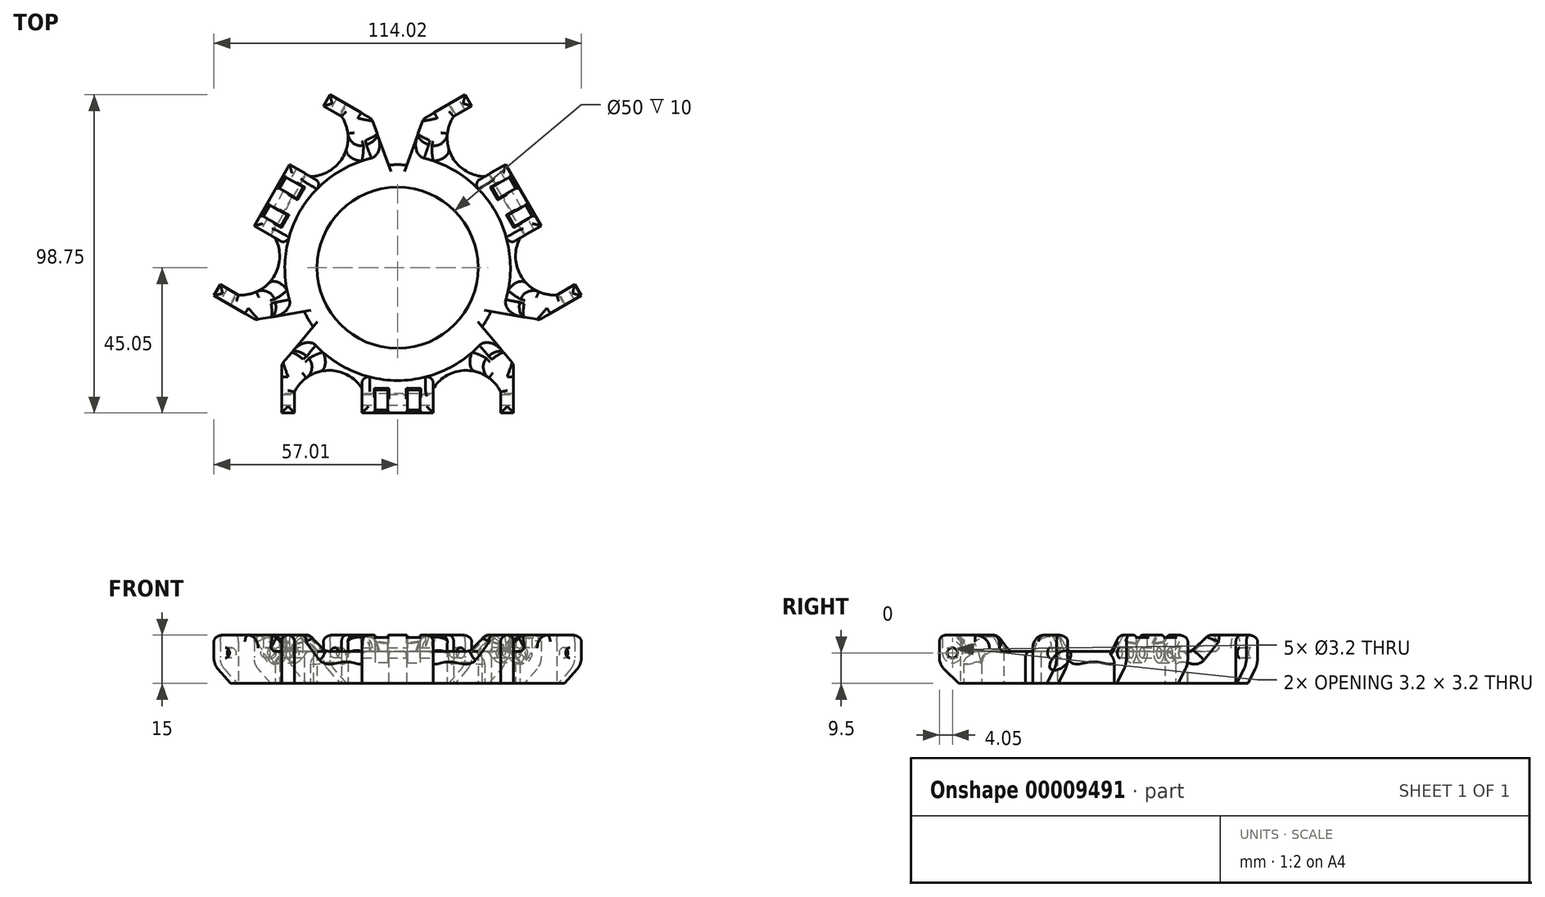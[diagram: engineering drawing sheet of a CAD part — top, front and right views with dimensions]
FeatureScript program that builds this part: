
annotation { "Feature Type Name" : "Feature", "Feature Type Description" : "" }
export const myFeature = defineFeature(function(context is Context, id is Id, definition is map)
    precondition{}
    {
        {
            assignVariable(context, id + "F0", {"name" : "JointHeight", "anyValue" : 18});
        }
        {
            var Q0;
            Q0=qCreatedBy(makeId("Top.planeOp"),FACE);
            var sketch = newSketch(context, id + "F1", { "sketchPlane" : qUnion([Q0])});
            skCircle(sketch, "E0", {"center": v(0, 0) * mm, "radius": 25 * mm});
            skCircle(sketch, "E1", {"center": v(0, 0) * mm, "radius": 32 * mm});
            skSolve(sketch);
        }
        {
            var Q0;
            Q0=qCreatedBy(makeId("Top.planeOp"),FACE);
            var sketch = newSketch(context, id + "F2", { "sketchPlane" : qUnion([Q0])});
            skLineSegment(sketch, "E2", {"start": v(-21.5, 50) * mm, "end": v(-21.5, -50) * mm, "construction": true});
            skLineSegment(sketch, "E3", {"start": v(21.5, 50) * mm, "end": v(21.5, -50) * mm, "construction": true});
            skLineSegment(sketch, "E4", {"start": v(-11, -50) * mm, "end": v(-11, -30.05) * mm, "construction": true});
            skLineSegment(sketch, "E5", {"start": v(11, -50) * mm, "end": v(11, -30.05) * mm, "construction": true});
            skLineSegment(sketch, "E6", {"start": v(-32, -50) * mm, "end": v(-32, 0) * mm, "construction": true});
            skLineSegment(sketch, "E7", {"start": v(32, -50) * mm, "end": v(32, 0) * mm, "construction": true});
            skLineSegment(sketch, "E8", {"start": v(0, -41.5) * mm, "end": v(0, -32) * mm, "construction": true});
            skLineSegment(sketch, "E9", {"start": v(-11, -30.05) * mm, "end": v(-11, -45.05) * mm});
            skLineSegment(sketch, "E10", {"start": v(-11, -45.05) * mm, "end": v(11, -45.05) * mm});
            skLineSegment(sketch, "E11", {"start": v(11, -45.05) * mm, "end": v(11, -30.05) * mm});
            skLineSegment(sketch, "E12", {"start": v(-32, -45.05) * mm, "end": v(-36, -45.05) * mm});
            skArc(sketch, "E13", {"start": v(-11, -30.05) * mm, "mid": v(0, -32) * mm, "end": v(11, -30.05) * mm});
            skLineSegment(sketch, "E14", {"start": v(-36, -45.05) * mm, "end": v(-36, -30.05) * mm});
            skLineSegment(sketch, "E15", {"start": v(-36, -30.05) * mm, "end": v(-26.2, -18.37) * mm});
            skCircle(sketch, "E16", {"center": v(-21.5, -41.5) * mm, "radius": 9.25 * mm, "construction": true});
            skLineSegment(sketch, "E17", {"start": v(-32, -45.05) * mm, "end": v(-32, -38.55) * mm});
            skArc(sketch, "E18", {"start": v(-11, -37.55) * mm, "mid": v(-21.8, -31.88) * mm, "end": v(-32, -38.55) * mm});
            skArc(sketch, "E19", {"start": v(-26.2, -18.37) * mm, "mid": v(-19.5, -25.38) * mm, "end": v(-11, -30.05) * mm});
            skLineSegment(sketch, "E20.MirrorCS", {"start": v(36, -45.05) * mm, "end": v(36, -30.05) * mm});
            skLineSegment(sketch, "E21.MirrorCS", {"start": v(32, -45.05) * mm, "end": v(36, -45.05) * mm});
            skLineSegment(sketch, "E22.MirrorCS", {"start": v(36, -30.05) * mm, "end": v(26.2, -18.37) * mm});
            skLineSegment(sketch, "E23.MirrorCS", {"start": v(32, -45.05) * mm, "end": v(32, -38.55) * mm});
            skArc(sketch, "E24.MirrorCS", {"start": v(11, -37.55) * mm, "mid": v(21.8, -31.88) * mm, "end": v(32, -38.55) * mm});
            skArc(sketch, "E25.MirrorCS", {"start": v(26.2, -18.37) * mm, "mid": v(19.5, -25.38) * mm, "end": v(11, -30.05) * mm});
            skSolve(sketch);
        }
        {
            var Q0;
            Q0=makeQuery(id+"F1.imprint","IMPRINT",FACE,{"disambiguationData":[TD([[makeQuery(id+"F1.imprint","IMPRINT",EDGE,{"derivedFrom":sQuery(id+"F1.wireOp",EDGE,"E0")}),-1.0]])]});
            extrude(context, id + "F3", {"entities" : qUnion([Q0]), "depth" : 10 * mm});
        }
        {
            var Q0;
            Q0 = qSketchRegion(id + "F2", true);
            extrude(context, id + "F4", {"entities" : qUnion([Q0]), "depth" : (getVariable(context, 'JointHeight') - 3) * mm});
        }
        {
            var Q0;
            Q0=makeQuery(id+"F4.opExtrude","SWEPT_FACE",FACE,{"disambiguationData":[OSD([sQuery(id+"F2.wireOp",EDGE,"E20.MirrorCS")])]});
            var sketch = newSketch(context, id + "F5", { "sketchPlane" : qUnion([Q0])});
            skCircle(sketch, "E26", {"center": v(-41, 9.5) * mm, "radius": 1.6 * mm});
            skSolve(sketch);
        }
        {
            var Q0;
            Q0=makeQuery(id+"F5.imprint","IMPRINT",FACE,{"disambiguationData":[TD([[makeQuery(id+"F5.imprint","IMPRINT",EDGE,{"derivedFrom":sQuery(id+"F5.wireOp",EDGE,"E26")}),1.0]])]});
            var Q1;
            Q1=makeQuery(id+"F4.opExtrude","SWEPT_FACE",FACE,{"disambiguationData":[OSD([sQuery(id+"F2.wireOp",EDGE,"E14")])]});
            extrude(context, id + "F6", {"entities" : qUnion([Q0]), "operationType" : NewBodyOperationType.REMOVE, "endBound" : BoundingType.UP_TO_SURFACE, "oppositeDirection" : true, "endBoundEntityFace" : qUnion([Q1]), "depth" : 25 * mm});
        }
        {
            var Q0;
            Q0=makeQuery(id+"F4.opExtrude","SWEPT_BODY",BODY,{"disambiguationData":[OSD([sQuery(id+"F2.wireOp",EDGE,"E9"),sQuery(id+"F2.wireOp",EDGE,"E10"),sQuery(id+"F2.wireOp",EDGE,"E11"),sQuery(id+"F2.wireOp",EDGE,"E12"),sQuery(id+"F2.wireOp",EDGE,"E13"),sQuery(id+"F2.wireOp",EDGE,"E14"),sQuery(id+"F2.wireOp",EDGE,"E15"),sQuery(id+"F2.wireOp",EDGE,"E17"),sQuery(id+"F2.wireOp",EDGE,"E18"),sQuery(id+"F2.wireOp",EDGE,"E19"),sQuery(id+"F2.wireOp",EDGE,"E20.MirrorCS"),sQuery(id+"F2.wireOp",EDGE,"E21.MirrorCS"),sQuery(id+"F2.wireOp",EDGE,"E22.MirrorCS"),sQuery(id+"F2.wireOp",EDGE,"E23.MirrorCS"),sQuery(id+"F2.wireOp",EDGE,"E24.MirrorCS"),sQuery(id+"F2.wireOp",EDGE,"E25.MirrorCS")])]});
            var Q1;
            Q1=makeQuery(id+"F3.opExtrude","SWEPT_FACE",FACE,{"disambiguationData":[OSD([sQuery(id+"F1.wireOp",EDGE,"E1")])]});
            circularPattern(context, id + "F7", {"operationType" : NewBodyOperationType.ADD, "entities" : qUnion([Q0]), "axis" : qUnion([Q1]), "angle" : 120 * degree, "instanceCount" : 3});
        }
        {
            var Q0;
            Q0=makeQuery(id+"F4.opExtrude","CAP_EDGE",EDGE,{"disambiguationData":[OSD([sQuery(id+"F2.wireOp",EDGE,"E13"),sQuery(id+"F2.wireOp",EDGE,"E19"),sQuery(id+"F2.wireOp",EDGE,"E25.MirrorCS")])],"isStart":false});
            var Q1;
            Q1=makeQuery(id+"F7.opPattern","COPY",EDGE,{"derivedFrom":makeQuery(id+"F4.opExtrude","CAP_EDGE",EDGE,{"disambiguationData":[OSD([sQuery(id+"F2.wireOp",EDGE,"E13"),sQuery(id+"F2.wireOp",EDGE,"E19"),sQuery(id+"F2.wireOp",EDGE,"E25.MirrorCS")])],"isStart":false}),"instanceName":"1"});
            var Q2;
            Q2=makeQuery(id+"F7.opPattern","COPY",EDGE,{"derivedFrom":makeQuery(id+"F4.opExtrude","CAP_EDGE",EDGE,{"disambiguationData":[OSD([sQuery(id+"F2.wireOp",EDGE,"E13"),sQuery(id+"F2.wireOp",EDGE,"E19"),sQuery(id+"F2.wireOp",EDGE,"E25.MirrorCS")])],"isStart":false}),"instanceName":"2"});
            chamfer(context, id + "F8", {"entities" : qUnion([Q0, Q1, Q2]), "width" : 8 * mm});
        }
        {
            var Q0;
            Q0=makeQuery(id+"F8.opChamfer","BLEND_EDGE",EDGE,{"blendedFrom":[makeQuery(id+"F4.opExtrude","CAP_EDGE",EDGE,{"disambiguationData":[OSD([sQuery(id+"F2.wireOp",EDGE,"E13"),sQuery(id+"F2.wireOp",EDGE,"E19"),sQuery(id+"F2.wireOp",EDGE,"E25.MirrorCS")])],"isStart":false}),makeQuery(id+"F4.opExtrude","SWEPT_FACE",FACE,{"disambiguationData":[OSD([sQuery(id+"F2.wireOp",EDGE,"E24.MirrorCS")])]})],"blendedInto":[makeQuery(id+"F4.opExtrude","SWEPT_FACE",FACE,{"disambiguationData":[OSD([sQuery(id+"F2.wireOp",EDGE,"E24.MirrorCS")])]})]});
            var Q1;
            Q1=makeQuery(id+"F8.opChamfer","BLEND_EDGE",EDGE,{"blendedFrom":[makeQuery(id+"F4.opExtrude","CAP_EDGE",EDGE,{"disambiguationData":[OSD([sQuery(id+"F2.wireOp",EDGE,"E13"),sQuery(id+"F2.wireOp",EDGE,"E19"),sQuery(id+"F2.wireOp",EDGE,"E25.MirrorCS")])],"isStart":false}),makeQuery(id+"F4.opExtrude","SWEPT_FACE",FACE,{"disambiguationData":[OSD([sQuery(id+"F2.wireOp",EDGE,"E18")])]})],"blendedInto":[makeQuery(id+"F4.opExtrude","SWEPT_FACE",FACE,{"disambiguationData":[OSD([sQuery(id+"F2.wireOp",EDGE,"E18")])]})]});
            var Q2;
            Q2=makeQuery(id+"F8.opChamfer","BLEND_EDGE",EDGE,{"blendedFrom":[makeQuery(id+"F4.opExtrude","CAP_EDGE",EDGE,{"disambiguationData":[OSD([sQuery(id+"F2.wireOp",EDGE,"E13"),sQuery(id+"F2.wireOp",EDGE,"E19"),sQuery(id+"F2.wireOp",EDGE,"E25.MirrorCS")])],"isStart":false}),makeQuery(id+"F4.opExtrude","SWEPT_FACE",FACE,{"disambiguationData":[OSD([sQuery(id+"F2.wireOp",EDGE,"E22.MirrorCS")])]})],"blendedInto":[makeQuery(id+"F4.opExtrude","SWEPT_FACE",FACE,{"disambiguationData":[OSD([sQuery(id+"F2.wireOp",EDGE,"E22.MirrorCS")])]})]});
            var Q3;
            Q3=makeQuery(id+"F8.opChamfer","BLEND_EDGE",EDGE,{"blendedFrom":[makeQuery(id+"F4.opExtrude","CAP_EDGE",EDGE,{"disambiguationData":[OSD([sQuery(id+"F2.wireOp",EDGE,"E13"),sQuery(id+"F2.wireOp",EDGE,"E19"),sQuery(id+"F2.wireOp",EDGE,"E25.MirrorCS")])],"isStart":false}),makeQuery(id+"F4.opExtrude","SWEPT_FACE",FACE,{"disambiguationData":[OSD([sQuery(id+"F2.wireOp",EDGE,"E15")])]})],"blendedInto":[makeQuery(id+"F4.opExtrude","SWEPT_FACE",FACE,{"disambiguationData":[OSD([sQuery(id+"F2.wireOp",EDGE,"E15")])]})]});
            var Q4;
            Q4=makeQuery(id+"F8.opChamfer","BLEND_EDGE",EDGE,{"blendedFrom":[makeQuery(id+"F7.opPattern","COPY",EDGE,{"derivedFrom":makeQuery(id+"F4.opExtrude","CAP_EDGE",EDGE,{"disambiguationData":[OSD([sQuery(id+"F2.wireOp",EDGE,"E13"),sQuery(id+"F2.wireOp",EDGE,"E19"),sQuery(id+"F2.wireOp",EDGE,"E25.MirrorCS")])],"isStart":false}),"instanceName":"2"}),makeQuery(id+"F7.opPattern","COPY",FACE,{"derivedFrom":makeQuery(id+"F4.opExtrude","SWEPT_FACE",FACE,{"disambiguationData":[OSD([sQuery(id+"F2.wireOp",EDGE,"E18")])]}),"instanceName":"2"})],"blendedInto":[makeQuery(id+"F7.opPattern","COPY",FACE,{"derivedFrom":makeQuery(id+"F4.opExtrude","SWEPT_FACE",FACE,{"disambiguationData":[OSD([sQuery(id+"F2.wireOp",EDGE,"E18")])]}),"instanceName":"2"})]});
            var Q5;
            Q5=makeQuery(id+"F8.opChamfer","BLEND_EDGE",EDGE,{"blendedFrom":[makeQuery(id+"F7.opPattern","COPY",EDGE,{"derivedFrom":makeQuery(id+"F4.opExtrude","CAP_EDGE",EDGE,{"disambiguationData":[OSD([sQuery(id+"F2.wireOp",EDGE,"E13"),sQuery(id+"F2.wireOp",EDGE,"E19"),sQuery(id+"F2.wireOp",EDGE,"E25.MirrorCS")])],"isStart":false}),"instanceName":"1"}),makeQuery(id+"F7.opPattern","COPY",FACE,{"derivedFrom":makeQuery(id+"F4.opExtrude","SWEPT_FACE",FACE,{"disambiguationData":[OSD([sQuery(id+"F2.wireOp",EDGE,"E24.MirrorCS")])]}),"instanceName":"1"})],"blendedInto":[makeQuery(id+"F7.opPattern","COPY",FACE,{"derivedFrom":makeQuery(id+"F4.opExtrude","SWEPT_FACE",FACE,{"disambiguationData":[OSD([sQuery(id+"F2.wireOp",EDGE,"E24.MirrorCS")])]}),"instanceName":"1"})]});
            var Q6;
            Q6=makeQuery(id+"F8.opChamfer","BLEND_EDGE",EDGE,{"blendedFrom":[makeQuery(id+"F7.opPattern","COPY",EDGE,{"derivedFrom":makeQuery(id+"F4.opExtrude","CAP_EDGE",EDGE,{"disambiguationData":[OSD([sQuery(id+"F2.wireOp",EDGE,"E13"),sQuery(id+"F2.wireOp",EDGE,"E19"),sQuery(id+"F2.wireOp",EDGE,"E25.MirrorCS")])],"isStart":false}),"instanceName":"1"}),makeQuery(id+"F7.opPattern","COPY",FACE,{"derivedFrom":makeQuery(id+"F4.opExtrude","SWEPT_FACE",FACE,{"disambiguationData":[OSD([sQuery(id+"F2.wireOp",EDGE,"E18")])]}),"instanceName":"1"})],"blendedInto":[makeQuery(id+"F7.opPattern","COPY",FACE,{"derivedFrom":makeQuery(id+"F4.opExtrude","SWEPT_FACE",FACE,{"disambiguationData":[OSD([sQuery(id+"F2.wireOp",EDGE,"E18")])]}),"instanceName":"1"})]});
            var Q7;
            Q7=makeQuery(id+"F8.opChamfer","BLEND_EDGE",EDGE,{"blendedFrom":[makeQuery(id+"F7.opPattern","COPY",EDGE,{"derivedFrom":makeQuery(id+"F4.opExtrude","CAP_EDGE",EDGE,{"disambiguationData":[OSD([sQuery(id+"F2.wireOp",EDGE,"E13"),sQuery(id+"F2.wireOp",EDGE,"E19"),sQuery(id+"F2.wireOp",EDGE,"E25.MirrorCS")])],"isStart":false}),"instanceName":"2"}),makeQuery(id+"F7.opPattern","COPY",FACE,{"derivedFrom":makeQuery(id+"F4.opExtrude","SWEPT_FACE",FACE,{"disambiguationData":[OSD([sQuery(id+"F2.wireOp",EDGE,"E24.MirrorCS")])]}),"instanceName":"2"})],"blendedInto":[makeQuery(id+"F7.opPattern","COPY",FACE,{"derivedFrom":makeQuery(id+"F4.opExtrude","SWEPT_FACE",FACE,{"disambiguationData":[OSD([sQuery(id+"F2.wireOp",EDGE,"E24.MirrorCS")])]}),"instanceName":"2"})]});
            var Q8;
            Q8=makeQuery(id+"F8.opChamfer","BLEND_EDGE",EDGE,{"blendedFrom":[makeQuery(id+"F7.opPattern","COPY",EDGE,{"derivedFrom":makeQuery(id+"F4.opExtrude","CAP_EDGE",EDGE,{"disambiguationData":[OSD([sQuery(id+"F2.wireOp",EDGE,"E13"),sQuery(id+"F2.wireOp",EDGE,"E19"),sQuery(id+"F2.wireOp",EDGE,"E25.MirrorCS")])],"isStart":false}),"instanceName":"1"}),makeQuery(id+"F7.opPattern","COPY",FACE,{"derivedFrom":makeQuery(id+"F4.opExtrude","SWEPT_FACE",FACE,{"disambiguationData":[OSD([sQuery(id+"F2.wireOp",EDGE,"E22.MirrorCS")])]}),"instanceName":"1"})],"blendedInto":[makeQuery(id+"F7.opPattern","COPY",FACE,{"derivedFrom":makeQuery(id+"F4.opExtrude","SWEPT_FACE",FACE,{"disambiguationData":[OSD([sQuery(id+"F2.wireOp",EDGE,"E22.MirrorCS")])]}),"instanceName":"1"})]});
            var Q9;
            Q9=makeQuery(id+"F8.opChamfer","BLEND_EDGE",EDGE,{"blendedFrom":[makeQuery(id+"F7.opPattern","COPY",EDGE,{"derivedFrom":makeQuery(id+"F4.opExtrude","CAP_EDGE",EDGE,{"disambiguationData":[OSD([sQuery(id+"F2.wireOp",EDGE,"E13"),sQuery(id+"F2.wireOp",EDGE,"E19"),sQuery(id+"F2.wireOp",EDGE,"E25.MirrorCS")])],"isStart":false}),"instanceName":"1"}),makeQuery(id+"F7.opPattern","COPY",FACE,{"derivedFrom":makeQuery(id+"F4.opExtrude","SWEPT_FACE",FACE,{"disambiguationData":[OSD([sQuery(id+"F2.wireOp",EDGE,"E15")])]}),"instanceName":"1"})],"blendedInto":[makeQuery(id+"F7.opPattern","COPY",FACE,{"derivedFrom":makeQuery(id+"F4.opExtrude","SWEPT_FACE",FACE,{"disambiguationData":[OSD([sQuery(id+"F2.wireOp",EDGE,"E15")])]}),"instanceName":"1"})]});
            var Q10;
            Q10=makeQuery(id+"F8.opChamfer","BLEND_EDGE",EDGE,{"blendedFrom":[makeQuery(id+"F7.opPattern","COPY",EDGE,{"derivedFrom":makeQuery(id+"F4.opExtrude","CAP_EDGE",EDGE,{"disambiguationData":[OSD([sQuery(id+"F2.wireOp",EDGE,"E13"),sQuery(id+"F2.wireOp",EDGE,"E19"),sQuery(id+"F2.wireOp",EDGE,"E25.MirrorCS")])],"isStart":false}),"instanceName":"2"}),makeQuery(id+"F7.opPattern","COPY",FACE,{"derivedFrom":makeQuery(id+"F4.opExtrude","SWEPT_FACE",FACE,{"disambiguationData":[OSD([sQuery(id+"F2.wireOp",EDGE,"E22.MirrorCS")])]}),"instanceName":"2"})],"blendedInto":[makeQuery(id+"F7.opPattern","COPY",FACE,{"derivedFrom":makeQuery(id+"F4.opExtrude","SWEPT_FACE",FACE,{"disambiguationData":[OSD([sQuery(id+"F2.wireOp",EDGE,"E22.MirrorCS")])]}),"instanceName":"2"})]});
            var Q11;
            Q11=makeQuery(id+"F7.opPattern","COPY",EDGE,{"derivedFrom":makeQuery(id+"F4.opExtrude","CAP_EDGE",EDGE,{"disambiguationData":[OSD([sQuery(id+"F2.wireOp",EDGE,"E15")])],"isStart":false}),"instanceName":"2"});
            var Q12;
            Q12=makeQuery(id+"F4.opExtrude","CAP_EDGE",EDGE,{"disambiguationData":[OSD([sQuery(id+"F2.wireOp",EDGE,"E22.MirrorCS")])],"isStart":false});
            var Q13;
            Q13=makeQuery(id+"F8.opChamfer","BLEND_EDGE",EDGE,{"blendedFrom":[makeQuery(id+"F7.opPattern","COPY",EDGE,{"derivedFrom":makeQuery(id+"F4.opExtrude","CAP_EDGE",EDGE,{"disambiguationData":[OSD([sQuery(id+"F2.wireOp",EDGE,"E13"),sQuery(id+"F2.wireOp",EDGE,"E19"),sQuery(id+"F2.wireOp",EDGE,"E25.MirrorCS")])],"isStart":false}),"instanceName":"2"}),makeQuery(id+"F7.opPattern","COPY",FACE,{"derivedFrom":makeQuery(id+"F4.opExtrude","SWEPT_FACE",FACE,{"disambiguationData":[OSD([sQuery(id+"F2.wireOp",EDGE,"E15")])]}),"instanceName":"2"})],"blendedInto":[makeQuery(id+"F7.opPattern","COPY",FACE,{"derivedFrom":makeQuery(id+"F4.opExtrude","SWEPT_FACE",FACE,{"disambiguationData":[OSD([sQuery(id+"F2.wireOp",EDGE,"E15")])]}),"instanceName":"2"})]});
            var Q14;
            {var subQ0=sQuery(id+"F1.wireOp",EDGE,"E1");Q14=makeQuery(id+"F8.opChamfer","TWEAK_EDGE",EDGE,{"derivedFrom":[makeQuery(id+"F7.boolean.opBoolean","TWEAK_VERTEX",VERTEX,{"derivedFrom":[makeQuery(id+"F3.opExtrude","CAP_FACE",FACE,{"disambiguationData":[OSD([sQuery(id+"F1.wireOp",EDGE,"E0"),subQ0])],"isStart":false}),makeQuery(id+"F3.opExtrude","SWEPT_FACE",FACE,{"disambiguationData":[OSD([subQ0])]}),makeQuery(id+"F7.opPattern","COPY",FACE,{"derivedFrom":makeQuery(id+"F4.opExtrude","SWEPT_FACE",FACE,{"disambiguationData":[OSD([sQuery(id+"F2.wireOp",EDGE,"E13"),sQuery(id+"F2.wireOp",EDGE,"E19"),sQuery(id+"F2.wireOp",EDGE,"E25.MirrorCS")])]}),"instanceName":"2"}),makeQuery(id+"F7.opPattern","COPY",FACE,{"derivedFrom":makeQuery(id+"F4.opExtrude","SWEPT_FACE",FACE,{"disambiguationData":[OSD([sQuery(id+"F2.wireOp",EDGE,"E22.MirrorCS")])]}),"instanceName":"2"})]})]});}
            var Q15;
            {var subQ0=sQuery(id+"F1.wireOp",EDGE,"E1");Q15=makeQuery(id+"F8.opChamfer","TWEAK_EDGE",EDGE,{"derivedFrom":[makeQuery(id+"F7.boolean.opBoolean","TWEAK_VERTEX",VERTEX,{"derivedFrom":[makeQuery(id+"F3.opExtrude","CAP_FACE",FACE,{"disambiguationData":[OSD([sQuery(id+"F1.wireOp",EDGE,"E0"),subQ0])],"isStart":false}),makeQuery(id+"F3.opExtrude","SWEPT_FACE",FACE,{"disambiguationData":[OSD([subQ0])]}),makeQuery(id+"F7.opPattern","COPY",FACE,{"derivedFrom":makeQuery(id+"F4.opExtrude","SWEPT_FACE",FACE,{"disambiguationData":[OSD([sQuery(id+"F2.wireOp",EDGE,"E13"),sQuery(id+"F2.wireOp",EDGE,"E19"),sQuery(id+"F2.wireOp",EDGE,"E25.MirrorCS")])]}),"instanceName":"1"}),makeQuery(id+"F7.opPattern","COPY",FACE,{"derivedFrom":makeQuery(id+"F4.opExtrude","SWEPT_FACE",FACE,{"disambiguationData":[OSD([sQuery(id+"F2.wireOp",EDGE,"E15")])]}),"instanceName":"1"})]})]});}
            var Q16;
            {var subQ0=sQuery(id+"F1.wireOp",EDGE,"E1");Q16=makeQuery(id+"F8.opChamfer","TWEAK_EDGE",EDGE,{"derivedFrom":[makeQuery(id+"F7.boolean.opBoolean","TWEAK_VERTEX",VERTEX,{"derivedFrom":[makeQuery(id+"F3.opExtrude","CAP_FACE",FACE,{"disambiguationData":[OSD([sQuery(id+"F1.wireOp",EDGE,"E0"),subQ0])],"isStart":false}),makeQuery(id+"F3.opExtrude","SWEPT_FACE",FACE,{"disambiguationData":[OSD([subQ0])]}),makeQuery(id+"F7.opPattern","COPY",FACE,{"derivedFrom":makeQuery(id+"F4.opExtrude","SWEPT_FACE",FACE,{"disambiguationData":[OSD([sQuery(id+"F2.wireOp",EDGE,"E13"),sQuery(id+"F2.wireOp",EDGE,"E19"),sQuery(id+"F2.wireOp",EDGE,"E25.MirrorCS")])]}),"instanceName":"1"}),makeQuery(id+"F7.opPattern","COPY",FACE,{"derivedFrom":makeQuery(id+"F4.opExtrude","SWEPT_FACE",FACE,{"disambiguationData":[OSD([sQuery(id+"F2.wireOp",EDGE,"E22.MirrorCS")])]}),"instanceName":"1"})]})]});}
            var Q17;
            {var subQ0=sQuery(id+"F1.wireOp",EDGE,"E1");Q17=makeQuery(id+"F8.opChamfer","TWEAK_EDGE",EDGE,{"derivedFrom":[makeQuery(id+"F7.boolean.opBoolean","TWEAK_VERTEX",VERTEX,{"derivedFrom":[makeQuery(id+"F3.opExtrude","CAP_FACE",FACE,{"disambiguationData":[OSD([sQuery(id+"F1.wireOp",EDGE,"E0"),subQ0])],"isStart":false}),makeQuery(id+"F3.opExtrude","SWEPT_FACE",FACE,{"disambiguationData":[OSD([subQ0])]}),makeQuery(id+"F4.opExtrude","SWEPT_FACE",FACE,{"disambiguationData":[OSD([sQuery(id+"F2.wireOp",EDGE,"E13"),sQuery(id+"F2.wireOp",EDGE,"E19"),sQuery(id+"F2.wireOp",EDGE,"E25.MirrorCS")])]}),makeQuery(id+"F4.opExtrude","SWEPT_FACE",FACE,{"disambiguationData":[OSD([sQuery(id+"F2.wireOp",EDGE,"E15")])]})]})]});}
            var Q18;
            Q18=makeQuery(id+"F4.opExtrude","CAP_EDGE",EDGE,{"disambiguationData":[OSD([sQuery(id+"F2.wireOp",EDGE,"E15")])],"isStart":false});
            var Q19;
            Q19=makeQuery(id+"F7.opPattern","COPY",EDGE,{"derivedFrom":makeQuery(id+"F4.opExtrude","CAP_EDGE",EDGE,{"disambiguationData":[OSD([sQuery(id+"F2.wireOp",EDGE,"E22.MirrorCS")])],"isStart":false}),"instanceName":"1"});
            var Q20;
            Q20=makeQuery(id+"F7.opPattern","COPY",EDGE,{"derivedFrom":makeQuery(id+"F4.opExtrude","CAP_EDGE",EDGE,{"disambiguationData":[OSD([sQuery(id+"F2.wireOp",EDGE,"E22.MirrorCS")])],"isStart":false}),"instanceName":"2"});
            var Q21;
            Q21=makeQuery(id+"F7.opPattern","COPY",EDGE,{"derivedFrom":makeQuery(id+"F4.opExtrude","CAP_EDGE",EDGE,{"disambiguationData":[OSD([sQuery(id+"F2.wireOp",EDGE,"E15")])],"isStart":false}),"instanceName":"1"});
            var Q22;
            {var subQ0=sQuery(id+"F1.wireOp",EDGE,"E1");Q22=makeQuery(id+"F8.opChamfer","TWEAK_EDGE",EDGE,{"derivedFrom":[makeQuery(id+"F7.boolean.opBoolean","TWEAK_VERTEX",VERTEX,{"derivedFrom":[makeQuery(id+"F3.opExtrude","CAP_FACE",FACE,{"disambiguationData":[OSD([sQuery(id+"F1.wireOp",EDGE,"E0"),subQ0])],"isStart":false}),makeQuery(id+"F3.opExtrude","SWEPT_FACE",FACE,{"disambiguationData":[OSD([subQ0])]}),makeQuery(id+"F7.opPattern","COPY",FACE,{"derivedFrom":makeQuery(id+"F4.opExtrude","SWEPT_FACE",FACE,{"disambiguationData":[OSD([sQuery(id+"F2.wireOp",EDGE,"E13"),sQuery(id+"F2.wireOp",EDGE,"E19"),sQuery(id+"F2.wireOp",EDGE,"E25.MirrorCS")])]}),"instanceName":"2"}),makeQuery(id+"F7.opPattern","COPY",FACE,{"derivedFrom":makeQuery(id+"F4.opExtrude","SWEPT_FACE",FACE,{"disambiguationData":[OSD([sQuery(id+"F2.wireOp",EDGE,"E15")])]}),"instanceName":"2"})]})]});}
            var Q23;
            {var subQ0=sQuery(id+"F1.wireOp",EDGE,"E1");Q23=makeQuery(id+"F8.opChamfer","TWEAK_EDGE",EDGE,{"derivedFrom":[makeQuery(id+"F7.boolean.opBoolean","TWEAK_VERTEX",VERTEX,{"derivedFrom":[makeQuery(id+"F3.opExtrude","CAP_FACE",FACE,{"disambiguationData":[OSD([sQuery(id+"F1.wireOp",EDGE,"E0"),subQ0])],"isStart":false}),makeQuery(id+"F3.opExtrude","SWEPT_FACE",FACE,{"disambiguationData":[OSD([subQ0])]}),makeQuery(id+"F4.opExtrude","SWEPT_FACE",FACE,{"disambiguationData":[OSD([sQuery(id+"F2.wireOp",EDGE,"E13"),sQuery(id+"F2.wireOp",EDGE,"E19"),sQuery(id+"F2.wireOp",EDGE,"E25.MirrorCS")])]}),makeQuery(id+"F4.opExtrude","SWEPT_FACE",FACE,{"disambiguationData":[OSD([sQuery(id+"F2.wireOp",EDGE,"E22.MirrorCS")])]})]})]});}
            fillet(context, id + "F9", {"entities" : qUnion([Q0, Q1, Q2, Q3, Q4, Q5, Q6, Q7, Q8, Q9, Q10, Q11, Q12, Q13, Q14, Q15, Q16, Q17, Q18, Q19, Q20, Q21, Q22, Q23]), "radius" : 4 * mm, "tangentPropagation" : true, "allowEdgeOverflow" : false});
        }
        {
            var Q0;
            Q0=makeQuery(id+"F8.opChamfer","BLEND_EDGE",EDGE,{"blendedFrom":[makeQuery(id+"F7.opPattern","COPY",EDGE,{"derivedFrom":makeQuery(id+"F4.opExtrude","CAP_EDGE",EDGE,{"disambiguationData":[OSD([sQuery(id+"F2.wireOp",EDGE,"E13"),sQuery(id+"F2.wireOp",EDGE,"E19"),sQuery(id+"F2.wireOp",EDGE,"E25.MirrorCS")])],"isStart":false}),"instanceName":"1"}),makeQuery(id+"F7.opPattern","COPY",FACE,{"derivedFrom":makeQuery(id+"F4.opExtrude","SWEPT_FACE",FACE,{"disambiguationData":[OSD([sQuery(id+"F2.wireOp",EDGE,"E11")])]}),"instanceName":"1"})],"blendedInto":[makeQuery(id+"F7.opPattern","COPY",FACE,{"derivedFrom":makeQuery(id+"F4.opExtrude","SWEPT_FACE",FACE,{"disambiguationData":[OSD([sQuery(id+"F2.wireOp",EDGE,"E11")])]}),"instanceName":"1"})]});
            var Q1;
            Q1=makeQuery(id+"F8.opChamfer","BLEND_EDGE",EDGE,{"blendedFrom":[makeQuery(id+"F7.opPattern","COPY",EDGE,{"derivedFrom":makeQuery(id+"F4.opExtrude","CAP_EDGE",EDGE,{"disambiguationData":[OSD([sQuery(id+"F2.wireOp",EDGE,"E13"),sQuery(id+"F2.wireOp",EDGE,"E19"),sQuery(id+"F2.wireOp",EDGE,"E25.MirrorCS")])],"isStart":false}),"instanceName":"1"}),makeQuery(id+"F7.opPattern","COPY",FACE,{"derivedFrom":makeQuery(id+"F4.opExtrude","SWEPT_FACE",FACE,{"disambiguationData":[OSD([sQuery(id+"F2.wireOp",EDGE,"E9")])]}),"instanceName":"1"})],"blendedInto":[makeQuery(id+"F7.opPattern","COPY",FACE,{"derivedFrom":makeQuery(id+"F4.opExtrude","SWEPT_FACE",FACE,{"disambiguationData":[OSD([sQuery(id+"F2.wireOp",EDGE,"E9")])]}),"instanceName":"1"})]});
            var Q2;
            Q2=makeQuery(id+"F8.opChamfer","BLEND_EDGE",EDGE,{"blendedFrom":[makeQuery(id+"F7.opPattern","COPY",EDGE,{"derivedFrom":makeQuery(id+"F4.opExtrude","CAP_EDGE",EDGE,{"disambiguationData":[OSD([sQuery(id+"F2.wireOp",EDGE,"E13"),sQuery(id+"F2.wireOp",EDGE,"E19"),sQuery(id+"F2.wireOp",EDGE,"E25.MirrorCS")])],"isStart":false}),"instanceName":"2"}),makeQuery(id+"F7.opPattern","COPY",FACE,{"derivedFrom":makeQuery(id+"F4.opExtrude","SWEPT_FACE",FACE,{"disambiguationData":[OSD([sQuery(id+"F2.wireOp",EDGE,"E11")])]}),"instanceName":"2"})],"blendedInto":[makeQuery(id+"F7.opPattern","COPY",FACE,{"derivedFrom":makeQuery(id+"F4.opExtrude","SWEPT_FACE",FACE,{"disambiguationData":[OSD([sQuery(id+"F2.wireOp",EDGE,"E11")])]}),"instanceName":"2"})]});
            var Q3;
            Q3=makeQuery(id+"F8.opChamfer","BLEND_EDGE",EDGE,{"blendedFrom":[makeQuery(id+"F7.opPattern","COPY",EDGE,{"derivedFrom":makeQuery(id+"F4.opExtrude","CAP_EDGE",EDGE,{"disambiguationData":[OSD([sQuery(id+"F2.wireOp",EDGE,"E13"),sQuery(id+"F2.wireOp",EDGE,"E19"),sQuery(id+"F2.wireOp",EDGE,"E25.MirrorCS")])],"isStart":false}),"instanceName":"2"}),makeQuery(id+"F7.opPattern","COPY",FACE,{"derivedFrom":makeQuery(id+"F4.opExtrude","SWEPT_FACE",FACE,{"disambiguationData":[OSD([sQuery(id+"F2.wireOp",EDGE,"E9")])]}),"instanceName":"2"})],"blendedInto":[makeQuery(id+"F7.opPattern","COPY",FACE,{"derivedFrom":makeQuery(id+"F4.opExtrude","SWEPT_FACE",FACE,{"disambiguationData":[OSD([sQuery(id+"F2.wireOp",EDGE,"E9")])]}),"instanceName":"2"})]});
            var Q4;
            Q4=makeQuery(id+"F8.opChamfer","BLEND_EDGE",EDGE,{"blendedFrom":[makeQuery(id+"F4.opExtrude","CAP_EDGE",EDGE,{"disambiguationData":[OSD([sQuery(id+"F2.wireOp",EDGE,"E13"),sQuery(id+"F2.wireOp",EDGE,"E19"),sQuery(id+"F2.wireOp",EDGE,"E25.MirrorCS")])],"isStart":false}),makeQuery(id+"F4.opExtrude","SWEPT_FACE",FACE,{"disambiguationData":[OSD([sQuery(id+"F2.wireOp",EDGE,"E11")])]})],"blendedInto":[makeQuery(id+"F4.opExtrude","SWEPT_FACE",FACE,{"disambiguationData":[OSD([sQuery(id+"F2.wireOp",EDGE,"E11")])]})]});
            var Q5;
            Q5=makeQuery(id+"F8.opChamfer","BLEND_EDGE",EDGE,{"blendedFrom":[makeQuery(id+"F4.opExtrude","CAP_EDGE",EDGE,{"disambiguationData":[OSD([sQuery(id+"F2.wireOp",EDGE,"E13"),sQuery(id+"F2.wireOp",EDGE,"E19"),sQuery(id+"F2.wireOp",EDGE,"E25.MirrorCS")])],"isStart":false}),makeQuery(id+"F4.opExtrude","SWEPT_FACE",FACE,{"disambiguationData":[OSD([sQuery(id+"F2.wireOp",EDGE,"E9")])]})],"blendedInto":[makeQuery(id+"F4.opExtrude","SWEPT_FACE",FACE,{"disambiguationData":[OSD([sQuery(id+"F2.wireOp",EDGE,"E9")])]})]});
            var Q6;
            Q6=makeQuery(id+"F8.opChamfer","SPLIT",FACE,{"disambiguationData":[OD(0.0)],"derivedFrom":makeQuery(id+"F4.opExtrude","CAP_FACE",FACE,{"disambiguationData":[OSD([sQuery(id+"F2.wireOp",EDGE,"E9"),sQuery(id+"F2.wireOp",EDGE,"E10"),sQuery(id+"F2.wireOp",EDGE,"E11"),sQuery(id+"F2.wireOp",EDGE,"E12"),sQuery(id+"F2.wireOp",EDGE,"E13"),sQuery(id+"F2.wireOp",EDGE,"E14"),sQuery(id+"F2.wireOp",EDGE,"E15"),sQuery(id+"F2.wireOp",EDGE,"E17"),sQuery(id+"F2.wireOp",EDGE,"E18"),sQuery(id+"F2.wireOp",EDGE,"E19"),sQuery(id+"F2.wireOp",EDGE,"E20.MirrorCS"),sQuery(id+"F2.wireOp",EDGE,"E21.MirrorCS"),sQuery(id+"F2.wireOp",EDGE,"E22.MirrorCS"),sQuery(id+"F2.wireOp",EDGE,"E23.MirrorCS"),sQuery(id+"F2.wireOp",EDGE,"E24.MirrorCS"),sQuery(id+"F2.wireOp",EDGE,"E25.MirrorCS")])],"isStart":false})});
            var Q7;
            Q7=makeQuery(id+"F8.opChamfer","SPLIT",FACE,{"disambiguationData":[OD(1.0)],"derivedFrom":makeQuery(id+"F4.opExtrude","CAP_FACE",FACE,{"disambiguationData":[OSD([sQuery(id+"F2.wireOp",EDGE,"E9"),sQuery(id+"F2.wireOp",EDGE,"E10"),sQuery(id+"F2.wireOp",EDGE,"E11"),sQuery(id+"F2.wireOp",EDGE,"E12"),sQuery(id+"F2.wireOp",EDGE,"E13"),sQuery(id+"F2.wireOp",EDGE,"E14"),sQuery(id+"F2.wireOp",EDGE,"E15"),sQuery(id+"F2.wireOp",EDGE,"E17"),sQuery(id+"F2.wireOp",EDGE,"E18"),sQuery(id+"F2.wireOp",EDGE,"E19"),sQuery(id+"F2.wireOp",EDGE,"E20.MirrorCS"),sQuery(id+"F2.wireOp",EDGE,"E21.MirrorCS"),sQuery(id+"F2.wireOp",EDGE,"E22.MirrorCS"),sQuery(id+"F2.wireOp",EDGE,"E23.MirrorCS"),sQuery(id+"F2.wireOp",EDGE,"E24.MirrorCS"),sQuery(id+"F2.wireOp",EDGE,"E25.MirrorCS")])],"isStart":false})});
            var Q8;
            Q8=makeQuery(id+"F8.opChamfer","SPLIT",FACE,{"disambiguationData":[OD(2.0)],"derivedFrom":makeQuery(id+"F7.opPattern","COPY",FACE,{"derivedFrom":makeQuery(id+"F4.opExtrude","CAP_FACE",FACE,{"disambiguationData":[OSD([sQuery(id+"F2.wireOp",EDGE,"E9"),sQuery(id+"F2.wireOp",EDGE,"E10"),sQuery(id+"F2.wireOp",EDGE,"E11"),sQuery(id+"F2.wireOp",EDGE,"E12"),sQuery(id+"F2.wireOp",EDGE,"E13"),sQuery(id+"F2.wireOp",EDGE,"E14"),sQuery(id+"F2.wireOp",EDGE,"E15"),sQuery(id+"F2.wireOp",EDGE,"E17"),sQuery(id+"F2.wireOp",EDGE,"E18"),sQuery(id+"F2.wireOp",EDGE,"E19"),sQuery(id+"F2.wireOp",EDGE,"E20.MirrorCS"),sQuery(id+"F2.wireOp",EDGE,"E21.MirrorCS"),sQuery(id+"F2.wireOp",EDGE,"E22.MirrorCS"),sQuery(id+"F2.wireOp",EDGE,"E23.MirrorCS"),sQuery(id+"F2.wireOp",EDGE,"E24.MirrorCS"),sQuery(id+"F2.wireOp",EDGE,"E25.MirrorCS")])],"isStart":false}),"instanceName":"1"})});
            var Q9;
            Q9=makeQuery(id+"F8.opChamfer","SPLIT",FACE,{"disambiguationData":[OD(1.0)],"derivedFrom":makeQuery(id+"F7.opPattern","COPY",FACE,{"derivedFrom":makeQuery(id+"F4.opExtrude","CAP_FACE",FACE,{"disambiguationData":[OSD([sQuery(id+"F2.wireOp",EDGE,"E9"),sQuery(id+"F2.wireOp",EDGE,"E10"),sQuery(id+"F2.wireOp",EDGE,"E11"),sQuery(id+"F2.wireOp",EDGE,"E12"),sQuery(id+"F2.wireOp",EDGE,"E13"),sQuery(id+"F2.wireOp",EDGE,"E14"),sQuery(id+"F2.wireOp",EDGE,"E15"),sQuery(id+"F2.wireOp",EDGE,"E17"),sQuery(id+"F2.wireOp",EDGE,"E18"),sQuery(id+"F2.wireOp",EDGE,"E19"),sQuery(id+"F2.wireOp",EDGE,"E20.MirrorCS"),sQuery(id+"F2.wireOp",EDGE,"E21.MirrorCS"),sQuery(id+"F2.wireOp",EDGE,"E22.MirrorCS"),sQuery(id+"F2.wireOp",EDGE,"E23.MirrorCS"),sQuery(id+"F2.wireOp",EDGE,"E24.MirrorCS"),sQuery(id+"F2.wireOp",EDGE,"E25.MirrorCS")])],"isStart":false}),"instanceName":"1"})});
            var Q10;
            Q10=makeQuery(id+"F8.opChamfer","SPLIT",FACE,{"disambiguationData":[OD(0.0)],"derivedFrom":makeQuery(id+"F7.opPattern","COPY",FACE,{"derivedFrom":makeQuery(id+"F4.opExtrude","CAP_FACE",FACE,{"disambiguationData":[OSD([sQuery(id+"F2.wireOp",EDGE,"E9"),sQuery(id+"F2.wireOp",EDGE,"E10"),sQuery(id+"F2.wireOp",EDGE,"E11"),sQuery(id+"F2.wireOp",EDGE,"E12"),sQuery(id+"F2.wireOp",EDGE,"E13"),sQuery(id+"F2.wireOp",EDGE,"E14"),sQuery(id+"F2.wireOp",EDGE,"E15"),sQuery(id+"F2.wireOp",EDGE,"E17"),sQuery(id+"F2.wireOp",EDGE,"E18"),sQuery(id+"F2.wireOp",EDGE,"E19"),sQuery(id+"F2.wireOp",EDGE,"E20.MirrorCS"),sQuery(id+"F2.wireOp",EDGE,"E21.MirrorCS"),sQuery(id+"F2.wireOp",EDGE,"E22.MirrorCS"),sQuery(id+"F2.wireOp",EDGE,"E23.MirrorCS"),sQuery(id+"F2.wireOp",EDGE,"E24.MirrorCS"),sQuery(id+"F2.wireOp",EDGE,"E25.MirrorCS")])],"isStart":false}),"instanceName":"1"})});
            var Q11;
            Q11=makeQuery(id+"F8.opChamfer","SPLIT",FACE,{"disambiguationData":[OD(2.0)],"derivedFrom":makeQuery(id+"F7.opPattern","COPY",FACE,{"derivedFrom":makeQuery(id+"F4.opExtrude","CAP_FACE",FACE,{"disambiguationData":[OSD([sQuery(id+"F2.wireOp",EDGE,"E9"),sQuery(id+"F2.wireOp",EDGE,"E10"),sQuery(id+"F2.wireOp",EDGE,"E11"),sQuery(id+"F2.wireOp",EDGE,"E12"),sQuery(id+"F2.wireOp",EDGE,"E13"),sQuery(id+"F2.wireOp",EDGE,"E14"),sQuery(id+"F2.wireOp",EDGE,"E15"),sQuery(id+"F2.wireOp",EDGE,"E17"),sQuery(id+"F2.wireOp",EDGE,"E18"),sQuery(id+"F2.wireOp",EDGE,"E19"),sQuery(id+"F2.wireOp",EDGE,"E20.MirrorCS"),sQuery(id+"F2.wireOp",EDGE,"E21.MirrorCS"),sQuery(id+"F2.wireOp",EDGE,"E22.MirrorCS"),sQuery(id+"F2.wireOp",EDGE,"E23.MirrorCS"),sQuery(id+"F2.wireOp",EDGE,"E24.MirrorCS"),sQuery(id+"F2.wireOp",EDGE,"E25.MirrorCS")])],"isStart":false}),"instanceName":"2"})});
            var Q12;
            Q12=makeQuery(id+"F8.opChamfer","SPLIT",FACE,{"disambiguationData":[OD(0.0)],"derivedFrom":makeQuery(id+"F7.opPattern","COPY",FACE,{"derivedFrom":makeQuery(id+"F4.opExtrude","CAP_FACE",FACE,{"disambiguationData":[OSD([sQuery(id+"F2.wireOp",EDGE,"E9"),sQuery(id+"F2.wireOp",EDGE,"E10"),sQuery(id+"F2.wireOp",EDGE,"E11"),sQuery(id+"F2.wireOp",EDGE,"E12"),sQuery(id+"F2.wireOp",EDGE,"E13"),sQuery(id+"F2.wireOp",EDGE,"E14"),sQuery(id+"F2.wireOp",EDGE,"E15"),sQuery(id+"F2.wireOp",EDGE,"E17"),sQuery(id+"F2.wireOp",EDGE,"E18"),sQuery(id+"F2.wireOp",EDGE,"E19"),sQuery(id+"F2.wireOp",EDGE,"E20.MirrorCS"),sQuery(id+"F2.wireOp",EDGE,"E21.MirrorCS"),sQuery(id+"F2.wireOp",EDGE,"E22.MirrorCS"),sQuery(id+"F2.wireOp",EDGE,"E23.MirrorCS"),sQuery(id+"F2.wireOp",EDGE,"E24.MirrorCS"),sQuery(id+"F2.wireOp",EDGE,"E25.MirrorCS")])],"isStart":false}),"instanceName":"2"})});
            var Q13;
            Q13=makeQuery(id+"F8.opChamfer","SPLIT",FACE,{"disambiguationData":[OD(1.0)],"derivedFrom":makeQuery(id+"F7.opPattern","COPY",FACE,{"derivedFrom":makeQuery(id+"F4.opExtrude","CAP_FACE",FACE,{"disambiguationData":[OSD([sQuery(id+"F2.wireOp",EDGE,"E9"),sQuery(id+"F2.wireOp",EDGE,"E10"),sQuery(id+"F2.wireOp",EDGE,"E11"),sQuery(id+"F2.wireOp",EDGE,"E12"),sQuery(id+"F2.wireOp",EDGE,"E13"),sQuery(id+"F2.wireOp",EDGE,"E14"),sQuery(id+"F2.wireOp",EDGE,"E15"),sQuery(id+"F2.wireOp",EDGE,"E17"),sQuery(id+"F2.wireOp",EDGE,"E18"),sQuery(id+"F2.wireOp",EDGE,"E19"),sQuery(id+"F2.wireOp",EDGE,"E20.MirrorCS"),sQuery(id+"F2.wireOp",EDGE,"E21.MirrorCS"),sQuery(id+"F2.wireOp",EDGE,"E22.MirrorCS"),sQuery(id+"F2.wireOp",EDGE,"E23.MirrorCS"),sQuery(id+"F2.wireOp",EDGE,"E24.MirrorCS"),sQuery(id+"F2.wireOp",EDGE,"E25.MirrorCS")])],"isStart":false}),"instanceName":"2"})});
            var Q14;
            Q14=makeQuery(id+"F8.opChamfer","SPLIT",FACE,{"disambiguationData":[OD(2.0)],"derivedFrom":makeQuery(id+"F4.opExtrude","CAP_FACE",FACE,{"disambiguationData":[OSD([sQuery(id+"F2.wireOp",EDGE,"E9"),sQuery(id+"F2.wireOp",EDGE,"E10"),sQuery(id+"F2.wireOp",EDGE,"E11"),sQuery(id+"F2.wireOp",EDGE,"E12"),sQuery(id+"F2.wireOp",EDGE,"E13"),sQuery(id+"F2.wireOp",EDGE,"E14"),sQuery(id+"F2.wireOp",EDGE,"E15"),sQuery(id+"F2.wireOp",EDGE,"E17"),sQuery(id+"F2.wireOp",EDGE,"E18"),sQuery(id+"F2.wireOp",EDGE,"E19"),sQuery(id+"F2.wireOp",EDGE,"E20.MirrorCS"),sQuery(id+"F2.wireOp",EDGE,"E21.MirrorCS"),sQuery(id+"F2.wireOp",EDGE,"E22.MirrorCS"),sQuery(id+"F2.wireOp",EDGE,"E23.MirrorCS"),sQuery(id+"F2.wireOp",EDGE,"E24.MirrorCS"),sQuery(id+"F2.wireOp",EDGE,"E25.MirrorCS")])],"isStart":false})});
            fillet(context, id + "F10", {"entities" : qUnion([Q0, Q1, Q2, Q3, Q4, Q5, Q6, Q7, Q8, Q9, Q10, Q11, Q12, Q13, Q14]), "radius" : 2 * mm, "tangentPropagation" : true, "allowEdgeOverflow" : false});
        }
        {
            var Q0;
            {var subQ0=sQuery(id+"F1.wireOp",EDGE,"E1");Q0=makeQuery(id+"F8.opChamfer","TWEAK_EDGE",EDGE,{"derivedFrom":[makeQuery(id+"F7.boolean.opBoolean","TWEAK_VERTEX",VERTEX,{"derivedFrom":[makeQuery(id+"F3.opExtrude","CAP_FACE",FACE,{"disambiguationData":[OSD([sQuery(id+"F1.wireOp",EDGE,"E0"),subQ0])],"isStart":false}),makeQuery(id+"F3.opExtrude","SWEPT_FACE",FACE,{"disambiguationData":[OSD([subQ0])]}),makeQuery(id+"F4.opExtrude","SWEPT_FACE",FACE,{"disambiguationData":[OSD([sQuery(id+"F2.wireOp",EDGE,"E13"),sQuery(id+"F2.wireOp",EDGE,"E19"),sQuery(id+"F2.wireOp",EDGE,"E25.MirrorCS")])]}),makeQuery(id+"F4.opExtrude","SWEPT_FACE",FACE,{"disambiguationData":[OSD([sQuery(id+"F2.wireOp",EDGE,"E15")])]})]})]});}
            var Q1;
            {var subQ0=makeQuery(id+"F4.opExtrude","SWEPT_FACE",FACE,{"disambiguationData":[OSD([sQuery(id+"F2.wireOp",EDGE,"E13"),sQuery(id+"F2.wireOp",EDGE,"E19"),sQuery(id+"F2.wireOp",EDGE,"E25.MirrorCS")])]});var subQ1=sQuery(id+"F1.wireOp",EDGE,"E1");Q1=makeQuery(id+"F7.boolean.opBoolean","SPLIT",EDGE,{"disambiguationData":[TD([makeQuery(id+"F3.opExtrude","CAP_FACE",FACE,{"disambiguationData":[OSD([sQuery(id+"F1.wireOp",EDGE,"E0"),subQ1])],"isStart":false}),makeQuery(id+"F3.opExtrude","SWEPT_FACE",FACE,{"disambiguationData":[OSD([subQ1])]}),subQ0,makeQuery(id+"F4.opExtrude","SWEPT_FACE",FACE,{"disambiguationData":[OSD([sQuery(id+"F2.wireOp",EDGE,"E15")])]}),makeQuery(id+"F7.opPattern","COPY",FACE,{"derivedFrom":subQ0,"instanceName":"1"}),makeQuery(id+"F7.opPattern","COPY",FACE,{"derivedFrom":makeQuery(id+"F4.opExtrude","SWEPT_FACE",FACE,{"disambiguationData":[OSD([sQuery(id+"F2.wireOp",EDGE,"E22.MirrorCS")])]}),"instanceName":"1"})])],"derivedFrom":makeQuery(id+"F3.opExtrude","CAP_EDGE",EDGE,{"disambiguationData":[OSD([subQ1])],"isStart":false})});}
            var Q2;
            {var subQ0=sQuery(id+"F1.wireOp",EDGE,"E1");Q2=makeQuery(id+"F8.opChamfer","TWEAK_EDGE",EDGE,{"derivedFrom":[makeQuery(id+"F7.boolean.opBoolean","TWEAK_VERTEX",VERTEX,{"derivedFrom":[makeQuery(id+"F3.opExtrude","CAP_FACE",FACE,{"disambiguationData":[OSD([sQuery(id+"F1.wireOp",EDGE,"E0"),subQ0])],"isStart":false}),makeQuery(id+"F3.opExtrude","SWEPT_FACE",FACE,{"disambiguationData":[OSD([subQ0])]}),makeQuery(id+"F7.opPattern","COPY",FACE,{"derivedFrom":makeQuery(id+"F4.opExtrude","SWEPT_FACE",FACE,{"disambiguationData":[OSD([sQuery(id+"F2.wireOp",EDGE,"E13"),sQuery(id+"F2.wireOp",EDGE,"E19"),sQuery(id+"F2.wireOp",EDGE,"E25.MirrorCS")])]}),"instanceName":"1"}),makeQuery(id+"F7.opPattern","COPY",FACE,{"derivedFrom":makeQuery(id+"F4.opExtrude","SWEPT_FACE",FACE,{"disambiguationData":[OSD([sQuery(id+"F2.wireOp",EDGE,"E22.MirrorCS")])]}),"instanceName":"1"})]})]});}
            var Q3;
            {var subQ0=sQuery(id+"F1.wireOp",EDGE,"E1");var subQ1=sQuery(id+"F1.wireOp",EDGE,"E0");var subQ3=sQuery(id+"F2.wireOp",EDGE,"E19");var subQ5=sQuery(id+"F2.wireOp",EDGE,"E15");Q3=makeQuery(id+"F7.boolean.opBoolean","SPLIT",EDGE,{"disambiguationData":[TD([makeQuery(id+"F3.opExtrude","CAP_FACE",FACE,{"disambiguationData":[OSD([subQ1,subQ0])],"isStart":true})])],"derivedFrom":makeQuery(id+"F4.opExtrude","SWEPT_EDGE",EDGE,{"disambiguationData":[OSD([subQ5,subQ3])]})});}
            var Q4;
            {var subQ0=sQuery(id+"F1.wireOp",EDGE,"E1");var subQ1=sQuery(id+"F1.wireOp",EDGE,"E0");var subQ2=sQuery(id+"F2.wireOp",EDGE,"E25.MirrorCS");var subQ3=sQuery(id+"F2.wireOp",EDGE,"E22.MirrorCS");Q4=makeQuery(id+"F7.boolean.opBoolean","SPLIT",EDGE,{"disambiguationData":[TD([makeQuery(id+"F3.opExtrude","CAP_FACE",FACE,{"disambiguationData":[OSD([subQ1,subQ0])],"isStart":true})])],"derivedFrom":makeQuery(id+"F7.opPattern","COPY",EDGE,{"derivedFrom":makeQuery(id+"F4.opExtrude","SWEPT_EDGE",EDGE,{"disambiguationData":[OSD([subQ3,subQ2])]}),"instanceName":"1"})});}
            var Q5;
            {var subQ0=sQuery(id+"F1.wireOp",EDGE,"E1");Q5=makeQuery(id+"F8.opChamfer","TWEAK_EDGE",EDGE,{"derivedFrom":[makeQuery(id+"F7.boolean.opBoolean","TWEAK_VERTEX",VERTEX,{"derivedFrom":[makeQuery(id+"F3.opExtrude","CAP_FACE",FACE,{"disambiguationData":[OSD([sQuery(id+"F1.wireOp",EDGE,"E0"),subQ0])],"isStart":false}),makeQuery(id+"F3.opExtrude","SWEPT_FACE",FACE,{"disambiguationData":[OSD([subQ0])]}),makeQuery(id+"F7.opPattern","COPY",FACE,{"derivedFrom":makeQuery(id+"F4.opExtrude","SWEPT_FACE",FACE,{"disambiguationData":[OSD([sQuery(id+"F2.wireOp",EDGE,"E13"),sQuery(id+"F2.wireOp",EDGE,"E19"),sQuery(id+"F2.wireOp",EDGE,"E25.MirrorCS")])]}),"instanceName":"1"}),makeQuery(id+"F7.opPattern","COPY",FACE,{"derivedFrom":makeQuery(id+"F4.opExtrude","SWEPT_FACE",FACE,{"disambiguationData":[OSD([sQuery(id+"F2.wireOp",EDGE,"E15")])]}),"instanceName":"1"})]})]});}
            var Q6;
            {var subQ0=makeQuery(id+"F4.opExtrude","SWEPT_FACE",FACE,{"disambiguationData":[OSD([sQuery(id+"F2.wireOp",EDGE,"E13"),sQuery(id+"F2.wireOp",EDGE,"E19"),sQuery(id+"F2.wireOp",EDGE,"E25.MirrorCS")])]});var subQ1=sQuery(id+"F1.wireOp",EDGE,"E1");Q6=makeQuery(id+"F7.boolean.opBoolean","SPLIT",EDGE,{"disambiguationData":[TD([makeQuery(id+"F3.opExtrude","CAP_FACE",FACE,{"disambiguationData":[OSD([sQuery(id+"F1.wireOp",EDGE,"E0"),subQ1])],"isStart":false}),makeQuery(id+"F3.opExtrude","SWEPT_FACE",FACE,{"disambiguationData":[OSD([subQ1])]}),makeQuery(id+"F7.opPattern","COPY",FACE,{"derivedFrom":subQ0,"instanceName":"1"}),makeQuery(id+"F7.opPattern","COPY",FACE,{"derivedFrom":makeQuery(id+"F4.opExtrude","SWEPT_FACE",FACE,{"disambiguationData":[OSD([sQuery(id+"F2.wireOp",EDGE,"E15")])]}),"instanceName":"1"}),makeQuery(id+"F7.opPattern","COPY",FACE,{"derivedFrom":subQ0,"instanceName":"2"}),makeQuery(id+"F7.opPattern","COPY",FACE,{"derivedFrom":makeQuery(id+"F4.opExtrude","SWEPT_FACE",FACE,{"disambiguationData":[OSD([sQuery(id+"F2.wireOp",EDGE,"E22.MirrorCS")])]}),"instanceName":"2"})])],"derivedFrom":makeQuery(id+"F3.opExtrude","CAP_EDGE",EDGE,{"disambiguationData":[OSD([subQ1])],"isStart":false})});}
            var Q7;
            {var subQ0=sQuery(id+"F1.wireOp",EDGE,"E1");Q7=makeQuery(id+"F8.opChamfer","TWEAK_EDGE",EDGE,{"derivedFrom":[makeQuery(id+"F7.boolean.opBoolean","TWEAK_VERTEX",VERTEX,{"derivedFrom":[makeQuery(id+"F3.opExtrude","CAP_FACE",FACE,{"disambiguationData":[OSD([sQuery(id+"F1.wireOp",EDGE,"E0"),subQ0])],"isStart":false}),makeQuery(id+"F3.opExtrude","SWEPT_FACE",FACE,{"disambiguationData":[OSD([subQ0])]}),makeQuery(id+"F7.opPattern","COPY",FACE,{"derivedFrom":makeQuery(id+"F4.opExtrude","SWEPT_FACE",FACE,{"disambiguationData":[OSD([sQuery(id+"F2.wireOp",EDGE,"E13"),sQuery(id+"F2.wireOp",EDGE,"E19"),sQuery(id+"F2.wireOp",EDGE,"E25.MirrorCS")])]}),"instanceName":"2"}),makeQuery(id+"F7.opPattern","COPY",FACE,{"derivedFrom":makeQuery(id+"F4.opExtrude","SWEPT_FACE",FACE,{"disambiguationData":[OSD([sQuery(id+"F2.wireOp",EDGE,"E22.MirrorCS")])]}),"instanceName":"2"})]})]});}
            var Q8;
            {var subQ0=sQuery(id+"F1.wireOp",EDGE,"E1");var subQ1=sQuery(id+"F1.wireOp",EDGE,"E0");var subQ2=sQuery(id+"F2.wireOp",EDGE,"E25.MirrorCS");var subQ3=sQuery(id+"F2.wireOp",EDGE,"E22.MirrorCS");Q8=makeQuery(id+"F7.boolean.opBoolean","SPLIT",EDGE,{"disambiguationData":[TD([makeQuery(id+"F3.opExtrude","CAP_FACE",FACE,{"disambiguationData":[OSD([subQ1,subQ0])],"isStart":true})])],"derivedFrom":makeQuery(id+"F7.opPattern","COPY",EDGE,{"derivedFrom":makeQuery(id+"F4.opExtrude","SWEPT_EDGE",EDGE,{"disambiguationData":[OSD([subQ3,subQ2])]}),"instanceName":"2"})});}
            var Q9;
            {var subQ0=sQuery(id+"F1.wireOp",EDGE,"E1");var subQ1=sQuery(id+"F1.wireOp",EDGE,"E0");var subQ3=sQuery(id+"F2.wireOp",EDGE,"E19");var subQ4=sQuery(id+"F2.wireOp",EDGE,"E15");Q9=makeQuery(id+"F7.boolean.opBoolean","SPLIT",EDGE,{"disambiguationData":[TD([makeQuery(id+"F3.opExtrude","CAP_FACE",FACE,{"disambiguationData":[OSD([subQ1,subQ0])],"isStart":true})])],"derivedFrom":makeQuery(id+"F7.opPattern","COPY",EDGE,{"derivedFrom":makeQuery(id+"F4.opExtrude","SWEPT_EDGE",EDGE,{"disambiguationData":[OSD([subQ4,subQ3])]}),"instanceName":"1"})});}
            var Q10;
            {var subQ0=sQuery(id+"F1.wireOp",EDGE,"E1");var subQ1=sQuery(id+"F2.wireOp",EDGE,"E22.MirrorCS");var subQ2=sQuery(id+"F1.wireOp",EDGE,"E0");var subQ3=sQuery(id+"F2.wireOp",EDGE,"E25.MirrorCS");Q10=makeQuery(id+"F7.boolean.opBoolean","SPLIT",EDGE,{"disambiguationData":[TD([makeQuery(id+"F3.opExtrude","CAP_FACE",FACE,{"disambiguationData":[OSD([subQ2,subQ0])],"isStart":true})])],"derivedFrom":makeQuery(id+"F4.opExtrude","SWEPT_EDGE",EDGE,{"disambiguationData":[OSD([subQ1,subQ3])]})});}
            var Q11;
            {var subQ0=sQuery(id+"F1.wireOp",EDGE,"E1");var subQ1=sQuery(id+"F1.wireOp",EDGE,"E0");var subQ2=sQuery(id+"F2.wireOp",EDGE,"E15");var subQ4=sQuery(id+"F2.wireOp",EDGE,"E19");Q11=makeQuery(id+"F7.boolean.opBoolean","SPLIT",EDGE,{"disambiguationData":[TD([makeQuery(id+"F3.opExtrude","CAP_FACE",FACE,{"disambiguationData":[OSD([subQ1,subQ0])],"isStart":true})])],"derivedFrom":makeQuery(id+"F7.opPattern","COPY",EDGE,{"derivedFrom":makeQuery(id+"F4.opExtrude","SWEPT_EDGE",EDGE,{"disambiguationData":[OSD([subQ2,subQ4])]}),"instanceName":"2"})});}
            var Q12;
            {var subQ0=sQuery(id+"F1.wireOp",EDGE,"E1");var subQ1=makeQuery(id+"F4.opExtrude","SWEPT_FACE",FACE,{"disambiguationData":[OSD([sQuery(id+"F2.wireOp",EDGE,"E13"),sQuery(id+"F2.wireOp",EDGE,"E19"),sQuery(id+"F2.wireOp",EDGE,"E25.MirrorCS")])]});Q12=makeQuery(id+"F7.boolean.opBoolean","SPLIT",EDGE,{"disambiguationData":[TD([makeQuery(id+"F3.opExtrude","CAP_FACE",FACE,{"disambiguationData":[OSD([sQuery(id+"F1.wireOp",EDGE,"E0"),subQ0])],"isStart":false}),makeQuery(id+"F3.opExtrude","SWEPT_FACE",FACE,{"disambiguationData":[OSD([subQ0])]}),subQ1,makeQuery(id+"F4.opExtrude","SWEPT_FACE",FACE,{"disambiguationData":[OSD([sQuery(id+"F2.wireOp",EDGE,"E22.MirrorCS")])]}),makeQuery(id+"F7.opPattern","COPY",FACE,{"derivedFrom":subQ1,"instanceName":"2"}),makeQuery(id+"F7.opPattern","COPY",FACE,{"derivedFrom":makeQuery(id+"F4.opExtrude","SWEPT_FACE",FACE,{"disambiguationData":[OSD([sQuery(id+"F2.wireOp",EDGE,"E15")])]}),"instanceName":"2"})])],"derivedFrom":makeQuery(id+"F3.opExtrude","CAP_EDGE",EDGE,{"disambiguationData":[OSD([subQ0])],"isStart":false})});}
            var Q13;
            {var subQ0=sQuery(id+"F1.wireOp",EDGE,"E1");Q13=makeQuery(id+"F8.opChamfer","TWEAK_EDGE",EDGE,{"derivedFrom":[makeQuery(id+"F7.boolean.opBoolean","TWEAK_VERTEX",VERTEX,{"derivedFrom":[makeQuery(id+"F3.opExtrude","CAP_FACE",FACE,{"disambiguationData":[OSD([sQuery(id+"F1.wireOp",EDGE,"E0"),subQ0])],"isStart":false}),makeQuery(id+"F3.opExtrude","SWEPT_FACE",FACE,{"disambiguationData":[OSD([subQ0])]}),makeQuery(id+"F4.opExtrude","SWEPT_FACE",FACE,{"disambiguationData":[OSD([sQuery(id+"F2.wireOp",EDGE,"E13"),sQuery(id+"F2.wireOp",EDGE,"E19"),sQuery(id+"F2.wireOp",EDGE,"E25.MirrorCS")])]}),makeQuery(id+"F4.opExtrude","SWEPT_FACE",FACE,{"disambiguationData":[OSD([sQuery(id+"F2.wireOp",EDGE,"E22.MirrorCS")])]})]})]});}
            var Q14;
            {var subQ0=sQuery(id+"F1.wireOp",EDGE,"E1");Q14=makeQuery(id+"F8.opChamfer","TWEAK_EDGE",EDGE,{"derivedFrom":[makeQuery(id+"F7.boolean.opBoolean","TWEAK_VERTEX",VERTEX,{"derivedFrom":[makeQuery(id+"F3.opExtrude","CAP_FACE",FACE,{"disambiguationData":[OSD([sQuery(id+"F1.wireOp",EDGE,"E0"),subQ0])],"isStart":false}),makeQuery(id+"F3.opExtrude","SWEPT_FACE",FACE,{"disambiguationData":[OSD([subQ0])]}),makeQuery(id+"F7.opPattern","COPY",FACE,{"derivedFrom":makeQuery(id+"F4.opExtrude","SWEPT_FACE",FACE,{"disambiguationData":[OSD([sQuery(id+"F2.wireOp",EDGE,"E13"),sQuery(id+"F2.wireOp",EDGE,"E19"),sQuery(id+"F2.wireOp",EDGE,"E25.MirrorCS")])]}),"instanceName":"2"}),makeQuery(id+"F7.opPattern","COPY",FACE,{"derivedFrom":makeQuery(id+"F4.opExtrude","SWEPT_FACE",FACE,{"disambiguationData":[OSD([sQuery(id+"F2.wireOp",EDGE,"E15")])]}),"instanceName":"2"})]})]});}
            fillet(context, id + "F11", {"entities" : qUnion([Q0, Q1, Q2, Q3, Q4, Q5, Q6, Q7, Q8, Q9, Q10, Q11, Q12, Q13, Q14]), "radius" : 2 * mm, "tangentPropagation" : true, "allowEdgeOverflow" : false});
        }
        {
            var Q0;
            Q0=makeQuery(id+"F7.opPattern","COPY",EDGE,{"derivedFrom":makeQuery(id+"F4.opExtrude","CAP_EDGE",EDGE,{"disambiguationData":[OSD([sQuery(id+"F2.wireOp",EDGE,"E21.MirrorCS")])],"isStart":true}),"instanceName":"2"});
            var Q1;
            Q1=makeQuery(id+"F7.opPattern","COPY",EDGE,{"derivedFrom":makeQuery(id+"F4.opExtrude","CAP_EDGE",EDGE,{"disambiguationData":[OSD([sQuery(id+"F2.wireOp",EDGE,"E10")])],"isStart":true}),"instanceName":"2"});
            var Q2;
            Q2=makeQuery(id+"F7.opPattern","COPY",EDGE,{"derivedFrom":makeQuery(id+"F4.opExtrude","CAP_EDGE",EDGE,{"disambiguationData":[OSD([sQuery(id+"F2.wireOp",EDGE,"E12")])],"isStart":true}),"instanceName":"2"});
            var Q3;
            Q3=makeQuery(id+"F7.opPattern","COPY",EDGE,{"derivedFrom":makeQuery(id+"F4.opExtrude","CAP_EDGE",EDGE,{"disambiguationData":[OSD([sQuery(id+"F2.wireOp",EDGE,"E12")])],"isStart":true}),"instanceName":"1"});
            var Q4;
            Q4=makeQuery(id+"F7.opPattern","COPY",EDGE,{"derivedFrom":makeQuery(id+"F4.opExtrude","CAP_EDGE",EDGE,{"disambiguationData":[OSD([sQuery(id+"F2.wireOp",EDGE,"E10")])],"isStart":true}),"instanceName":"1"});
            var Q5;
            Q5=makeQuery(id+"F7.opPattern","COPY",EDGE,{"derivedFrom":makeQuery(id+"F4.opExtrude","CAP_EDGE",EDGE,{"disambiguationData":[OSD([sQuery(id+"F2.wireOp",EDGE,"E21.MirrorCS")])],"isStart":true}),"instanceName":"1"});
            var Q6;
            Q6=makeQuery(id+"F4.opExtrude","CAP_EDGE",EDGE,{"disambiguationData":[OSD([sQuery(id+"F2.wireOp",EDGE,"E12")])],"isStart":true});
            var Q7;
            Q7=makeQuery(id+"F4.opExtrude","CAP_EDGE",EDGE,{"disambiguationData":[OSD([sQuery(id+"F2.wireOp",EDGE,"E10")])],"isStart":true});
            var Q8;
            Q8=makeQuery(id+"F4.opExtrude","CAP_EDGE",EDGE,{"disambiguationData":[OSD([sQuery(id+"F2.wireOp",EDGE,"E21.MirrorCS")])],"isStart":true});
            chamfer(context, id + "F12", {"entities" : qUnion([Q0, Q1, Q2, Q3, Q4, Q5, Q6, Q7, Q8]), "width" : 6 * mm, "tangentPropagation" : true});
        }
        {
            var Q0;
            {var subQ0=sQuery(id+"F2.wireOp",EDGE,"E10");Q0=makeQuery(id+"F12.opChamfer","BLEND_EDGE",EDGE,{"blendedFrom":[makeQuery(id+"F7.opPattern","COPY",EDGE,{"derivedFrom":makeQuery(id+"F4.opExtrude","CAP_EDGE",EDGE,{"disambiguationData":[OSD([subQ0])],"isStart":true}),"instanceName":"1"}),makeQuery(id+"F7.opPattern","COPY",FACE,{"derivedFrom":makeQuery(id+"F4.opExtrude","SWEPT_FACE",FACE,{"disambiguationData":[OSD([subQ0])]}),"instanceName":"1"})],"blendedInto":[makeQuery(id+"F7.opPattern","COPY",FACE,{"derivedFrom":makeQuery(id+"F4.opExtrude","SWEPT_FACE",FACE,{"disambiguationData":[OSD([subQ0])]}),"instanceName":"1"})]});}
            var Q1;
            {var subQ0=sQuery(id+"F2.wireOp",EDGE,"E12");Q1=makeQuery(id+"F12.opChamfer","BLEND_EDGE",EDGE,{"blendedFrom":[makeQuery(id+"F7.opPattern","COPY",EDGE,{"derivedFrom":makeQuery(id+"F4.opExtrude","CAP_EDGE",EDGE,{"disambiguationData":[OSD([subQ0])],"isStart":true}),"instanceName":"1"}),makeQuery(id+"F7.opPattern","COPY",FACE,{"derivedFrom":makeQuery(id+"F4.opExtrude","SWEPT_FACE",FACE,{"disambiguationData":[OSD([subQ0])]}),"instanceName":"1"})],"blendedInto":[makeQuery(id+"F7.opPattern","COPY",FACE,{"derivedFrom":makeQuery(id+"F4.opExtrude","SWEPT_FACE",FACE,{"disambiguationData":[OSD([subQ0])]}),"instanceName":"1"})]});}
            var Q2;
            {var subQ0=sQuery(id+"F2.wireOp",EDGE,"E21.MirrorCS");Q2=makeQuery(id+"F12.opChamfer","BLEND_EDGE",EDGE,{"blendedFrom":[makeQuery(id+"F7.opPattern","COPY",EDGE,{"derivedFrom":makeQuery(id+"F4.opExtrude","CAP_EDGE",EDGE,{"disambiguationData":[OSD([subQ0])],"isStart":true}),"instanceName":"1"}),makeQuery(id+"F7.opPattern","COPY",FACE,{"derivedFrom":makeQuery(id+"F4.opExtrude","SWEPT_FACE",FACE,{"disambiguationData":[OSD([subQ0])]}),"instanceName":"1"})],"blendedInto":[makeQuery(id+"F7.opPattern","COPY",FACE,{"derivedFrom":makeQuery(id+"F4.opExtrude","SWEPT_FACE",FACE,{"disambiguationData":[OSD([subQ0])]}),"instanceName":"1"})]});}
            var Q3;
            {var subQ0=sQuery(id+"F2.wireOp",EDGE,"E12");Q3=makeQuery(id+"F12.opChamfer","BLEND_EDGE",EDGE,{"blendedFrom":[makeQuery(id+"F4.opExtrude","CAP_EDGE",EDGE,{"disambiguationData":[OSD([subQ0])],"isStart":true}),makeQuery(id+"F4.opExtrude","SWEPT_FACE",FACE,{"disambiguationData":[OSD([subQ0])]})],"blendedInto":[makeQuery(id+"F4.opExtrude","SWEPT_FACE",FACE,{"disambiguationData":[OSD([subQ0])]})]});}
            var Q4;
            {var subQ0=sQuery(id+"F2.wireOp",EDGE,"E10");Q4=makeQuery(id+"F12.opChamfer","BLEND_EDGE",EDGE,{"blendedFrom":[makeQuery(id+"F4.opExtrude","CAP_EDGE",EDGE,{"disambiguationData":[OSD([subQ0])],"isStart":true}),makeQuery(id+"F4.opExtrude","SWEPT_FACE",FACE,{"disambiguationData":[OSD([subQ0])]})],"blendedInto":[makeQuery(id+"F4.opExtrude","SWEPT_FACE",FACE,{"disambiguationData":[OSD([subQ0])]})]});}
            var Q5;
            {var subQ0=sQuery(id+"F2.wireOp",EDGE,"E21.MirrorCS");Q5=makeQuery(id+"F12.opChamfer","BLEND_EDGE",EDGE,{"blendedFrom":[makeQuery(id+"F4.opExtrude","CAP_EDGE",EDGE,{"disambiguationData":[OSD([subQ0])],"isStart":true}),makeQuery(id+"F4.opExtrude","SWEPT_FACE",FACE,{"disambiguationData":[OSD([subQ0])]})],"blendedInto":[makeQuery(id+"F4.opExtrude","SWEPT_FACE",FACE,{"disambiguationData":[OSD([subQ0])]})]});}
            var Q6;
            {var subQ0=sQuery(id+"F2.wireOp",EDGE,"E12");Q6=makeQuery(id+"F12.opChamfer","BLEND_EDGE",EDGE,{"blendedFrom":[makeQuery(id+"F7.opPattern","COPY",EDGE,{"derivedFrom":makeQuery(id+"F4.opExtrude","CAP_EDGE",EDGE,{"disambiguationData":[OSD([subQ0])],"isStart":true}),"instanceName":"2"}),makeQuery(id+"F7.opPattern","COPY",FACE,{"derivedFrom":makeQuery(id+"F4.opExtrude","SWEPT_FACE",FACE,{"disambiguationData":[OSD([subQ0])]}),"instanceName":"2"})],"blendedInto":[makeQuery(id+"F7.opPattern","COPY",FACE,{"derivedFrom":makeQuery(id+"F4.opExtrude","SWEPT_FACE",FACE,{"disambiguationData":[OSD([subQ0])]}),"instanceName":"2"})]});}
            var Q7;
            {var subQ0=sQuery(id+"F2.wireOp",EDGE,"E10");Q7=makeQuery(id+"F12.opChamfer","BLEND_EDGE",EDGE,{"blendedFrom":[makeQuery(id+"F7.opPattern","COPY",EDGE,{"derivedFrom":makeQuery(id+"F4.opExtrude","CAP_EDGE",EDGE,{"disambiguationData":[OSD([subQ0])],"isStart":true}),"instanceName":"2"}),makeQuery(id+"F7.opPattern","COPY",FACE,{"derivedFrom":makeQuery(id+"F4.opExtrude","SWEPT_FACE",FACE,{"disambiguationData":[OSD([subQ0])]}),"instanceName":"2"})],"blendedInto":[makeQuery(id+"F7.opPattern","COPY",FACE,{"derivedFrom":makeQuery(id+"F4.opExtrude","SWEPT_FACE",FACE,{"disambiguationData":[OSD([subQ0])]}),"instanceName":"2"})]});}
            var Q8;
            {var subQ0=sQuery(id+"F2.wireOp",EDGE,"E21.MirrorCS");Q8=makeQuery(id+"F12.opChamfer","BLEND_EDGE",EDGE,{"blendedFrom":[makeQuery(id+"F7.opPattern","COPY",EDGE,{"derivedFrom":makeQuery(id+"F4.opExtrude","CAP_EDGE",EDGE,{"disambiguationData":[OSD([subQ0])],"isStart":true}),"instanceName":"2"}),makeQuery(id+"F7.opPattern","COPY",FACE,{"derivedFrom":makeQuery(id+"F4.opExtrude","SWEPT_FACE",FACE,{"disambiguationData":[OSD([subQ0])]}),"instanceName":"2"})],"blendedInto":[makeQuery(id+"F7.opPattern","COPY",FACE,{"derivedFrom":makeQuery(id+"F4.opExtrude","SWEPT_FACE",FACE,{"disambiguationData":[OSD([subQ0])]}),"instanceName":"2"})]});}
            fillet(context, id + "F13", {"entities" : qUnion([Q0, Q1, Q2, Q3, Q4, Q5, Q6, Q7, Q8]), "radius" : 5 * mm, "tangentPropagation" : true, "allowEdgeOverflow" : false});
        }
        {
            var Q0;
            Q0=makeQuery(id+"F4.opExtrude","SWEPT_FACE",FACE,{"disambiguationData":[OSD([sQuery(id+"F2.wireOp",EDGE,"E11")])]});
            cPlane(context, id + "F14", {"entities" : qUnion([Q0]), "cplaneType" : CPlaneType.OFFSET, "offset" : 4 * mm, "oppositeDirection" : true, "width" : 150 * mm, "height" : 150 * mm});
        }
        {
            var Q0;
            Q0=qCreatedBy(id+"F14.planeOp",FACE);
            var sketch = newSketch(context, id + "F15", { "sketchPlane" : qUnion([Q0])});
            skCircle(sketch, "E27", {"center": v(-41, 9.5) * mm, "radius": 3.1 * mm});
            skLineSegment(sketch, "E28", {"start": v(-37.9, 9.5) * mm, "end": v(-37.9, 15.05) * mm});
            skLineSegment(sketch, "E29", {"start": v(-37.9, 15.05) * mm, "end": v(-44.1, 15.05) * mm});
            skLineSegment(sketch, "E30", {"start": v(-44.1, 15.05) * mm, "end": v(-44.1, 9.5) * mm});
            skSolve(sketch);
        }
        {
            var Q0;
            Q0 = qSketchRegion(id + "F15", true);
            extrude(context, id + "F16", {"entities" : qUnion([Q0]), "oppositeDirection" : true, "depth" : 4 * mm});
        }
        {
            var Q0;
            Q0=makeQuery(id+"F16.opExtrude","SWEPT_BODY",BODY,{"disambiguationData":[OSD([sQuery(id+"F15.wireOp",EDGE,"E27"),sQuery(id+"F15.wireOp",EDGE,"E28"),sQuery(id+"F15.wireOp",EDGE,"E29"),sQuery(id+"F15.wireOp",EDGE,"E30")])]});
            var Q1;
            Q1=qCreatedBy(makeId("Right.planeOp"),FACE);
            mirror(context, id + "F17", {"entities" : qUnion([Q0]), "mirrorPlane" : qUnion([Q1])});
        }
        {
            var Q0;
            Q0=makeQuery(id+"F17.opPattern","COPY",BODY,{"derivedFrom":makeQuery(id+"F16.opExtrude","SWEPT_BODY",BODY,{"disambiguationData":[OSD([sQuery(id+"F15.wireOp",EDGE,"E27"),sQuery(id+"F15.wireOp",EDGE,"E28"),sQuery(id+"F15.wireOp",EDGE,"E29"),sQuery(id+"F15.wireOp",EDGE,"E30")])]}),"instanceName":"1"});
            var Q1;
            Q1=makeQuery(id+"F16.opExtrude","SWEPT_BODY",BODY,{"disambiguationData":[OSD([sQuery(id+"F15.wireOp",EDGE,"E27"),sQuery(id+"F15.wireOp",EDGE,"E28"),sQuery(id+"F15.wireOp",EDGE,"E29"),sQuery(id+"F15.wireOp",EDGE,"E30")])]});
            var Q2;
            Q2=makeQuery(id+"F3.opExtrude","SWEPT_FACE",FACE,{"disambiguationData":[OSD([sQuery(id+"F1.wireOp",EDGE,"E0")])]});
            circularPattern(context, id + "F18", {"operationType" : NewBodyOperationType.REMOVE, "entities" : qUnion([Q0, Q1]), "axis" : qUnion([Q2]), "angle" : 120 * degree, "instanceCount" : 3});
        }
        {
            var Q0;
            {var subQ0=sQuery(id+"F2.wireOp",EDGE,"E10");Q0=makeQuery(id+"F18.boolean.opBoolean","INTERSECT",EDGE,{"derivedFrom":[makeQuery(id+"F10.opFillet","BLEND_FACE",FACE,{"disambiguationData":[OSD([subQ0]),TDD([makeQuery(id+"F4.opExtrude","CAP_EDGE",EDGE,{"disambiguationData":[OSD([subQ0])],"isStart":false})])]}),makeQuery(id+"F17.opPattern","COPY",FACE,{"derivedFrom":makeQuery(id+"F16.opExtrude","SWEPT_FACE",FACE,{"disambiguationData":[OSD([sQuery(id+"F15.wireOp",EDGE,"E30")])]}),"instanceName":"1"})]});}
            var Q1;
            {var subQ0=sQuery(id+"F2.wireOp",EDGE,"E25.MirrorCS");var subQ1=sQuery(id+"F2.wireOp",EDGE,"E19");var subQ2=sQuery(id+"F2.wireOp",EDGE,"E13");Q1=makeQuery(id+"F18.boolean.opBoolean","INTERSECT",EDGE,{"derivedFrom":[makeQuery(id+"F9.opFillet","SPLIT",FACE,{"disambiguationData":[OD(0.0)],"derivedFrom":makeQuery(id+"F8.opChamfer","BLEND_FACE",FACE,{"disambiguationData":[OSD([subQ2,subQ1,subQ0]),TDD([makeQuery(id+"F4.opExtrude","CAP_EDGE",EDGE,{"disambiguationData":[OSD([subQ2,subQ1,subQ0])],"isStart":false})])]})}),makeQuery(id+"F17.opPattern","COPY",FACE,{"derivedFrom":makeQuery(id+"F16.opExtrude","SWEPT_FACE",FACE,{"disambiguationData":[OSD([sQuery(id+"F15.wireOp",EDGE,"E28")])]}),"instanceName":"1"})]});}
            var Q2;
            {var subQ0=sQuery(id+"F2.wireOp",EDGE,"E25.MirrorCS");var subQ1=sQuery(id+"F2.wireOp",EDGE,"E19");var subQ2=sQuery(id+"F2.wireOp",EDGE,"E13");Q2=makeQuery(id+"F18.boolean.opBoolean","INTERSECT",EDGE,{"derivedFrom":[makeQuery(id+"F9.opFillet","SPLIT",FACE,{"disambiguationData":[OD(0.0)],"derivedFrom":makeQuery(id+"F8.opChamfer","BLEND_FACE",FACE,{"disambiguationData":[OSD([subQ2,subQ1,subQ0]),TDD([makeQuery(id+"F4.opExtrude","CAP_EDGE",EDGE,{"disambiguationData":[OSD([subQ2,subQ1,subQ0])],"isStart":false})])]})}),makeQuery(id+"F16.opExtrude","SWEPT_FACE",FACE,{"disambiguationData":[OSD([sQuery(id+"F15.wireOp",EDGE,"E28")])]})]});}
            var Q3;
            {var subQ0=sQuery(id+"F2.wireOp",EDGE,"E10");Q3=makeQuery(id+"F18.boolean.opBoolean","INTERSECT",EDGE,{"derivedFrom":[makeQuery(id+"F10.opFillet","BLEND_FACE",FACE,{"disambiguationData":[OSD([subQ0]),TDD([makeQuery(id+"F4.opExtrude","CAP_EDGE",EDGE,{"disambiguationData":[OSD([subQ0])],"isStart":false})])]}),makeQuery(id+"F16.opExtrude","SWEPT_FACE",FACE,{"disambiguationData":[OSD([sQuery(id+"F15.wireOp",EDGE,"E30")])]})]});}
            var Q4;
            Q4=makeQuery(id+"F18.boolean.opBoolean","INTERSECT",EDGE,{"derivedFrom":[makeQuery(id+"F8.opChamfer","SPLIT",FACE,{"disambiguationData":[OD(0.0)],"derivedFrom":makeQuery(id+"F4.opExtrude","CAP_FACE",FACE,{"disambiguationData":[OSD([sQuery(id+"F2.wireOp",EDGE,"E9"),sQuery(id+"F2.wireOp",EDGE,"E10"),sQuery(id+"F2.wireOp",EDGE,"E11"),sQuery(id+"F2.wireOp",EDGE,"E12"),sQuery(id+"F2.wireOp",EDGE,"E13"),sQuery(id+"F2.wireOp",EDGE,"E14"),sQuery(id+"F2.wireOp",EDGE,"E15"),sQuery(id+"F2.wireOp",EDGE,"E17"),sQuery(id+"F2.wireOp",EDGE,"E18"),sQuery(id+"F2.wireOp",EDGE,"E19"),sQuery(id+"F2.wireOp",EDGE,"E20.MirrorCS"),sQuery(id+"F2.wireOp",EDGE,"E21.MirrorCS"),sQuery(id+"F2.wireOp",EDGE,"E22.MirrorCS"),sQuery(id+"F2.wireOp",EDGE,"E23.MirrorCS"),sQuery(id+"F2.wireOp",EDGE,"E24.MirrorCS"),sQuery(id+"F2.wireOp",EDGE,"E25.MirrorCS")])],"isStart":false})}),makeQuery(id+"F16.opExtrude","CAP_FACE",FACE,{"disambiguationData":[OSD([sQuery(id+"F15.wireOp",EDGE,"E27"),sQuery(id+"F15.wireOp",EDGE,"E28"),sQuery(id+"F15.wireOp",EDGE,"E29"),sQuery(id+"F15.wireOp",EDGE,"E30")])],"isStart":false})]});
            var Q5;
            Q5=makeQuery(id+"F18.boolean.opBoolean","INTERSECT",EDGE,{"derivedFrom":[makeQuery(id+"F8.opChamfer","SPLIT",FACE,{"disambiguationData":[OD(0.0)],"derivedFrom":makeQuery(id+"F4.opExtrude","CAP_FACE",FACE,{"disambiguationData":[OSD([sQuery(id+"F2.wireOp",EDGE,"E9"),sQuery(id+"F2.wireOp",EDGE,"E10"),sQuery(id+"F2.wireOp",EDGE,"E11"),sQuery(id+"F2.wireOp",EDGE,"E12"),sQuery(id+"F2.wireOp",EDGE,"E13"),sQuery(id+"F2.wireOp",EDGE,"E14"),sQuery(id+"F2.wireOp",EDGE,"E15"),sQuery(id+"F2.wireOp",EDGE,"E17"),sQuery(id+"F2.wireOp",EDGE,"E18"),sQuery(id+"F2.wireOp",EDGE,"E19"),sQuery(id+"F2.wireOp",EDGE,"E20.MirrorCS"),sQuery(id+"F2.wireOp",EDGE,"E21.MirrorCS"),sQuery(id+"F2.wireOp",EDGE,"E22.MirrorCS"),sQuery(id+"F2.wireOp",EDGE,"E23.MirrorCS"),sQuery(id+"F2.wireOp",EDGE,"E24.MirrorCS"),sQuery(id+"F2.wireOp",EDGE,"E25.MirrorCS")])],"isStart":false})}),makeQuery(id+"F16.opExtrude","CAP_FACE",FACE,{"disambiguationData":[OSD([sQuery(id+"F15.wireOp",EDGE,"E27"),sQuery(id+"F15.wireOp",EDGE,"E28"),sQuery(id+"F15.wireOp",EDGE,"E29"),sQuery(id+"F15.wireOp",EDGE,"E30")])],"isStart":true})]});
            var Q6;
            Q6=makeQuery(id+"F18.boolean.opBoolean","INTERSECT",EDGE,{"derivedFrom":[makeQuery(id+"F8.opChamfer","SPLIT",FACE,{"disambiguationData":[OD(0.0)],"derivedFrom":makeQuery(id+"F4.opExtrude","CAP_FACE",FACE,{"disambiguationData":[OSD([sQuery(id+"F2.wireOp",EDGE,"E9"),sQuery(id+"F2.wireOp",EDGE,"E10"),sQuery(id+"F2.wireOp",EDGE,"E11"),sQuery(id+"F2.wireOp",EDGE,"E12"),sQuery(id+"F2.wireOp",EDGE,"E13"),sQuery(id+"F2.wireOp",EDGE,"E14"),sQuery(id+"F2.wireOp",EDGE,"E15"),sQuery(id+"F2.wireOp",EDGE,"E17"),sQuery(id+"F2.wireOp",EDGE,"E18"),sQuery(id+"F2.wireOp",EDGE,"E19"),sQuery(id+"F2.wireOp",EDGE,"E20.MirrorCS"),sQuery(id+"F2.wireOp",EDGE,"E21.MirrorCS"),sQuery(id+"F2.wireOp",EDGE,"E22.MirrorCS"),sQuery(id+"F2.wireOp",EDGE,"E23.MirrorCS"),sQuery(id+"F2.wireOp",EDGE,"E24.MirrorCS"),sQuery(id+"F2.wireOp",EDGE,"E25.MirrorCS")])],"isStart":false})}),makeQuery(id+"F17.opPattern","COPY",FACE,{"derivedFrom":makeQuery(id+"F16.opExtrude","CAP_FACE",FACE,{"disambiguationData":[OSD([sQuery(id+"F15.wireOp",EDGE,"E27"),sQuery(id+"F15.wireOp",EDGE,"E28"),sQuery(id+"F15.wireOp",EDGE,"E29"),sQuery(id+"F15.wireOp",EDGE,"E30")])],"isStart":false}),"instanceName":"1"})]});
            var Q7;
            Q7=makeQuery(id+"F18.boolean.opBoolean","INTERSECT",EDGE,{"derivedFrom":[makeQuery(id+"F8.opChamfer","SPLIT",FACE,{"disambiguationData":[OD(0.0)],"derivedFrom":makeQuery(id+"F4.opExtrude","CAP_FACE",FACE,{"disambiguationData":[OSD([sQuery(id+"F2.wireOp",EDGE,"E9"),sQuery(id+"F2.wireOp",EDGE,"E10"),sQuery(id+"F2.wireOp",EDGE,"E11"),sQuery(id+"F2.wireOp",EDGE,"E12"),sQuery(id+"F2.wireOp",EDGE,"E13"),sQuery(id+"F2.wireOp",EDGE,"E14"),sQuery(id+"F2.wireOp",EDGE,"E15"),sQuery(id+"F2.wireOp",EDGE,"E17"),sQuery(id+"F2.wireOp",EDGE,"E18"),sQuery(id+"F2.wireOp",EDGE,"E19"),sQuery(id+"F2.wireOp",EDGE,"E20.MirrorCS"),sQuery(id+"F2.wireOp",EDGE,"E21.MirrorCS"),sQuery(id+"F2.wireOp",EDGE,"E22.MirrorCS"),sQuery(id+"F2.wireOp",EDGE,"E23.MirrorCS"),sQuery(id+"F2.wireOp",EDGE,"E24.MirrorCS"),sQuery(id+"F2.wireOp",EDGE,"E25.MirrorCS")])],"isStart":false})}),makeQuery(id+"F17.opPattern","COPY",FACE,{"derivedFrom":makeQuery(id+"F16.opExtrude","CAP_FACE",FACE,{"disambiguationData":[OSD([sQuery(id+"F15.wireOp",EDGE,"E27"),sQuery(id+"F15.wireOp",EDGE,"E28"),sQuery(id+"F15.wireOp",EDGE,"E29"),sQuery(id+"F15.wireOp",EDGE,"E30")])],"isStart":true}),"instanceName":"1"})]});
            var Q8;
            {var subQ0=sQuery(id+"F2.wireOp",EDGE,"E10");Q8=makeQuery(id+"F18.boolean.opBoolean","INTERSECT",EDGE,{"derivedFrom":[makeQuery(id+"F10.opFillet","BLEND_FACE",FACE,{"disambiguationData":[OSD([subQ0]),TDD([makeQuery(id+"F7.opPattern","COPY",EDGE,{"derivedFrom":makeQuery(id+"F4.opExtrude","CAP_EDGE",EDGE,{"disambiguationData":[OSD([subQ0])],"isStart":false}),"instanceName":"2"})])]}),makeQuery(id+"F18.opPattern","COPY",FACE,{"derivedFrom":makeQuery(id+"F17.opPattern","COPY",FACE,{"derivedFrom":makeQuery(id+"F16.opExtrude","SWEPT_FACE",FACE,{"disambiguationData":[OSD([sQuery(id+"F15.wireOp",EDGE,"E30")])]}),"instanceName":"1"}),"instanceName":"1"})]});}
            var Q9;
            {var subQ0=sQuery(id+"F2.wireOp",EDGE,"E25.MirrorCS");var subQ1=sQuery(id+"F2.wireOp",EDGE,"E19");var subQ2=sQuery(id+"F2.wireOp",EDGE,"E13");Q9=makeQuery(id+"F18.boolean.opBoolean","INTERSECT",EDGE,{"derivedFrom":[makeQuery(id+"F9.opFillet","SPLIT",FACE,{"disambiguationData":[OD(0.0)],"derivedFrom":makeQuery(id+"F8.opChamfer","BLEND_FACE",FACE,{"disambiguationData":[OSD([subQ2,subQ1,subQ0]),TDD([makeQuery(id+"F7.opPattern","COPY",EDGE,{"derivedFrom":makeQuery(id+"F4.opExtrude","CAP_EDGE",EDGE,{"disambiguationData":[OSD([subQ2,subQ1,subQ0])],"isStart":false}),"instanceName":"2"})])]})}),makeQuery(id+"F18.opPattern","COPY",FACE,{"derivedFrom":makeQuery(id+"F17.opPattern","COPY",FACE,{"derivedFrom":makeQuery(id+"F16.opExtrude","SWEPT_FACE",FACE,{"disambiguationData":[OSD([sQuery(id+"F15.wireOp",EDGE,"E28")])]}),"instanceName":"1"}),"instanceName":"1"})]});}
            var Q10;
            Q10=makeQuery(id+"F18.boolean.opBoolean","INTERSECT",EDGE,{"derivedFrom":[makeQuery(id+"F8.opChamfer","SPLIT",FACE,{"disambiguationData":[OD(0.0)],"derivedFrom":makeQuery(id+"F7.opPattern","COPY",FACE,{"derivedFrom":makeQuery(id+"F4.opExtrude","CAP_FACE",FACE,{"disambiguationData":[OSD([sQuery(id+"F2.wireOp",EDGE,"E9"),sQuery(id+"F2.wireOp",EDGE,"E10"),sQuery(id+"F2.wireOp",EDGE,"E11"),sQuery(id+"F2.wireOp",EDGE,"E12"),sQuery(id+"F2.wireOp",EDGE,"E13"),sQuery(id+"F2.wireOp",EDGE,"E14"),sQuery(id+"F2.wireOp",EDGE,"E15"),sQuery(id+"F2.wireOp",EDGE,"E17"),sQuery(id+"F2.wireOp",EDGE,"E18"),sQuery(id+"F2.wireOp",EDGE,"E19"),sQuery(id+"F2.wireOp",EDGE,"E20.MirrorCS"),sQuery(id+"F2.wireOp",EDGE,"E21.MirrorCS"),sQuery(id+"F2.wireOp",EDGE,"E22.MirrorCS"),sQuery(id+"F2.wireOp",EDGE,"E23.MirrorCS"),sQuery(id+"F2.wireOp",EDGE,"E24.MirrorCS"),sQuery(id+"F2.wireOp",EDGE,"E25.MirrorCS")])],"isStart":false}),"instanceName":"2"})}),makeQuery(id+"F18.opPattern","COPY",FACE,{"derivedFrom":makeQuery(id+"F17.opPattern","COPY",FACE,{"derivedFrom":makeQuery(id+"F16.opExtrude","CAP_FACE",FACE,{"disambiguationData":[OSD([sQuery(id+"F15.wireOp",EDGE,"E27"),sQuery(id+"F15.wireOp",EDGE,"E28"),sQuery(id+"F15.wireOp",EDGE,"E29"),sQuery(id+"F15.wireOp",EDGE,"E30")])],"isStart":false}),"instanceName":"1"}),"instanceName":"1"})]});
            var Q11;
            Q11=makeQuery(id+"F18.boolean.opBoolean","INTERSECT",EDGE,{"derivedFrom":[makeQuery(id+"F8.opChamfer","SPLIT",FACE,{"disambiguationData":[OD(0.0)],"derivedFrom":makeQuery(id+"F7.opPattern","COPY",FACE,{"derivedFrom":makeQuery(id+"F4.opExtrude","CAP_FACE",FACE,{"disambiguationData":[OSD([sQuery(id+"F2.wireOp",EDGE,"E9"),sQuery(id+"F2.wireOp",EDGE,"E10"),sQuery(id+"F2.wireOp",EDGE,"E11"),sQuery(id+"F2.wireOp",EDGE,"E12"),sQuery(id+"F2.wireOp",EDGE,"E13"),sQuery(id+"F2.wireOp",EDGE,"E14"),sQuery(id+"F2.wireOp",EDGE,"E15"),sQuery(id+"F2.wireOp",EDGE,"E17"),sQuery(id+"F2.wireOp",EDGE,"E18"),sQuery(id+"F2.wireOp",EDGE,"E19"),sQuery(id+"F2.wireOp",EDGE,"E20.MirrorCS"),sQuery(id+"F2.wireOp",EDGE,"E21.MirrorCS"),sQuery(id+"F2.wireOp",EDGE,"E22.MirrorCS"),sQuery(id+"F2.wireOp",EDGE,"E23.MirrorCS"),sQuery(id+"F2.wireOp",EDGE,"E24.MirrorCS"),sQuery(id+"F2.wireOp",EDGE,"E25.MirrorCS")])],"isStart":false}),"instanceName":"2"})}),makeQuery(id+"F18.opPattern","COPY",FACE,{"derivedFrom":makeQuery(id+"F17.opPattern","COPY",FACE,{"derivedFrom":makeQuery(id+"F16.opExtrude","CAP_FACE",FACE,{"disambiguationData":[OSD([sQuery(id+"F15.wireOp",EDGE,"E27"),sQuery(id+"F15.wireOp",EDGE,"E28"),sQuery(id+"F15.wireOp",EDGE,"E29"),sQuery(id+"F15.wireOp",EDGE,"E30")])],"isStart":true}),"instanceName":"1"}),"instanceName":"1"})]});
            var Q12;
            Q12=makeQuery(id+"F18.boolean.opBoolean","INTERSECT",EDGE,{"derivedFrom":[makeQuery(id+"F8.opChamfer","SPLIT",FACE,{"disambiguationData":[OD(0.0)],"derivedFrom":makeQuery(id+"F7.opPattern","COPY",FACE,{"derivedFrom":makeQuery(id+"F4.opExtrude","CAP_FACE",FACE,{"disambiguationData":[OSD([sQuery(id+"F2.wireOp",EDGE,"E9"),sQuery(id+"F2.wireOp",EDGE,"E10"),sQuery(id+"F2.wireOp",EDGE,"E11"),sQuery(id+"F2.wireOp",EDGE,"E12"),sQuery(id+"F2.wireOp",EDGE,"E13"),sQuery(id+"F2.wireOp",EDGE,"E14"),sQuery(id+"F2.wireOp",EDGE,"E15"),sQuery(id+"F2.wireOp",EDGE,"E17"),sQuery(id+"F2.wireOp",EDGE,"E18"),sQuery(id+"F2.wireOp",EDGE,"E19"),sQuery(id+"F2.wireOp",EDGE,"E20.MirrorCS"),sQuery(id+"F2.wireOp",EDGE,"E21.MirrorCS"),sQuery(id+"F2.wireOp",EDGE,"E22.MirrorCS"),sQuery(id+"F2.wireOp",EDGE,"E23.MirrorCS"),sQuery(id+"F2.wireOp",EDGE,"E24.MirrorCS"),sQuery(id+"F2.wireOp",EDGE,"E25.MirrorCS")])],"isStart":false}),"instanceName":"2"})}),makeQuery(id+"F18.opPattern","COPY",FACE,{"derivedFrom":makeQuery(id+"F16.opExtrude","CAP_FACE",FACE,{"disambiguationData":[OSD([sQuery(id+"F15.wireOp",EDGE,"E27"),sQuery(id+"F15.wireOp",EDGE,"E28"),sQuery(id+"F15.wireOp",EDGE,"E29"),sQuery(id+"F15.wireOp",EDGE,"E30")])],"isStart":true}),"instanceName":"1"})]});
            var Q13;
            Q13=makeQuery(id+"F18.boolean.opBoolean","INTERSECT",EDGE,{"derivedFrom":[makeQuery(id+"F8.opChamfer","SPLIT",FACE,{"disambiguationData":[OD(0.0)],"derivedFrom":makeQuery(id+"F7.opPattern","COPY",FACE,{"derivedFrom":makeQuery(id+"F4.opExtrude","CAP_FACE",FACE,{"disambiguationData":[OSD([sQuery(id+"F2.wireOp",EDGE,"E9"),sQuery(id+"F2.wireOp",EDGE,"E10"),sQuery(id+"F2.wireOp",EDGE,"E11"),sQuery(id+"F2.wireOp",EDGE,"E12"),sQuery(id+"F2.wireOp",EDGE,"E13"),sQuery(id+"F2.wireOp",EDGE,"E14"),sQuery(id+"F2.wireOp",EDGE,"E15"),sQuery(id+"F2.wireOp",EDGE,"E17"),sQuery(id+"F2.wireOp",EDGE,"E18"),sQuery(id+"F2.wireOp",EDGE,"E19"),sQuery(id+"F2.wireOp",EDGE,"E20.MirrorCS"),sQuery(id+"F2.wireOp",EDGE,"E21.MirrorCS"),sQuery(id+"F2.wireOp",EDGE,"E22.MirrorCS"),sQuery(id+"F2.wireOp",EDGE,"E23.MirrorCS"),sQuery(id+"F2.wireOp",EDGE,"E24.MirrorCS"),sQuery(id+"F2.wireOp",EDGE,"E25.MirrorCS")])],"isStart":false}),"instanceName":"2"})}),makeQuery(id+"F18.opPattern","COPY",FACE,{"derivedFrom":makeQuery(id+"F16.opExtrude","CAP_FACE",FACE,{"disambiguationData":[OSD([sQuery(id+"F15.wireOp",EDGE,"E27"),sQuery(id+"F15.wireOp",EDGE,"E28"),sQuery(id+"F15.wireOp",EDGE,"E29"),sQuery(id+"F15.wireOp",EDGE,"E30")])],"isStart":false}),"instanceName":"1"})]});
            var Q14;
            {var subQ0=sQuery(id+"F2.wireOp",EDGE,"E10");Q14=makeQuery(id+"F18.boolean.opBoolean","INTERSECT",EDGE,{"derivedFrom":[makeQuery(id+"F10.opFillet","BLEND_FACE",FACE,{"disambiguationData":[OSD([subQ0]),TDD([makeQuery(id+"F7.opPattern","COPY",EDGE,{"derivedFrom":makeQuery(id+"F4.opExtrude","CAP_EDGE",EDGE,{"disambiguationData":[OSD([subQ0])],"isStart":false}),"instanceName":"2"})])]}),makeQuery(id+"F18.opPattern","COPY",FACE,{"derivedFrom":makeQuery(id+"F16.opExtrude","SWEPT_FACE",FACE,{"disambiguationData":[OSD([sQuery(id+"F15.wireOp",EDGE,"E30")])]}),"instanceName":"1"})]});}
            var Q15;
            {var subQ0=sQuery(id+"F2.wireOp",EDGE,"E25.MirrorCS");var subQ1=sQuery(id+"F2.wireOp",EDGE,"E19");var subQ2=sQuery(id+"F2.wireOp",EDGE,"E13");Q15=makeQuery(id+"F18.boolean.opBoolean","INTERSECT",EDGE,{"derivedFrom":[makeQuery(id+"F9.opFillet","SPLIT",FACE,{"disambiguationData":[OD(0.0)],"derivedFrom":makeQuery(id+"F8.opChamfer","BLEND_FACE",FACE,{"disambiguationData":[OSD([subQ2,subQ1,subQ0]),TDD([makeQuery(id+"F7.opPattern","COPY",EDGE,{"derivedFrom":makeQuery(id+"F4.opExtrude","CAP_EDGE",EDGE,{"disambiguationData":[OSD([subQ2,subQ1,subQ0])],"isStart":false}),"instanceName":"2"})])]})}),makeQuery(id+"F18.opPattern","COPY",FACE,{"derivedFrom":makeQuery(id+"F16.opExtrude","SWEPT_FACE",FACE,{"disambiguationData":[OSD([sQuery(id+"F15.wireOp",EDGE,"E28")])]}),"instanceName":"1"})]});}
            var Q16;
            {var subQ0=sQuery(id+"F2.wireOp",EDGE,"E10");Q16=makeQuery(id+"F18.boolean.opBoolean","INTERSECT",EDGE,{"derivedFrom":[makeQuery(id+"F10.opFillet","BLEND_FACE",FACE,{"disambiguationData":[OSD([subQ0]),TDD([makeQuery(id+"F7.opPattern","COPY",EDGE,{"derivedFrom":makeQuery(id+"F4.opExtrude","CAP_EDGE",EDGE,{"disambiguationData":[OSD([subQ0])],"isStart":false}),"instanceName":"1"})])]}),makeQuery(id+"F18.opPattern","COPY",FACE,{"derivedFrom":makeQuery(id+"F16.opExtrude","SWEPT_FACE",FACE,{"disambiguationData":[OSD([sQuery(id+"F15.wireOp",EDGE,"E30")])]}),"instanceName":"2"})]});}
            var Q17;
            {var subQ0=sQuery(id+"F2.wireOp",EDGE,"E25.MirrorCS");var subQ1=sQuery(id+"F2.wireOp",EDGE,"E19");var subQ2=sQuery(id+"F2.wireOp",EDGE,"E13");Q17=makeQuery(id+"F18.boolean.opBoolean","INTERSECT",EDGE,{"derivedFrom":[makeQuery(id+"F9.opFillet","SPLIT",FACE,{"disambiguationData":[OD(0.0)],"derivedFrom":makeQuery(id+"F8.opChamfer","BLEND_FACE",FACE,{"disambiguationData":[OSD([subQ2,subQ1,subQ0]),TDD([makeQuery(id+"F7.opPattern","COPY",EDGE,{"derivedFrom":makeQuery(id+"F4.opExtrude","CAP_EDGE",EDGE,{"disambiguationData":[OSD([subQ2,subQ1,subQ0])],"isStart":false}),"instanceName":"1"})])]})}),makeQuery(id+"F18.opPattern","COPY",FACE,{"derivedFrom":makeQuery(id+"F16.opExtrude","SWEPT_FACE",FACE,{"disambiguationData":[OSD([sQuery(id+"F15.wireOp",EDGE,"E28")])]}),"instanceName":"2"})]});}
            var Q18;
            Q18=makeQuery(id+"F18.boolean.opBoolean","INTERSECT",EDGE,{"derivedFrom":[makeQuery(id+"F8.opChamfer","SPLIT",FACE,{"disambiguationData":[OD(0.0)],"derivedFrom":makeQuery(id+"F7.opPattern","COPY",FACE,{"derivedFrom":makeQuery(id+"F4.opExtrude","CAP_FACE",FACE,{"disambiguationData":[OSD([sQuery(id+"F2.wireOp",EDGE,"E9"),sQuery(id+"F2.wireOp",EDGE,"E10"),sQuery(id+"F2.wireOp",EDGE,"E11"),sQuery(id+"F2.wireOp",EDGE,"E12"),sQuery(id+"F2.wireOp",EDGE,"E13"),sQuery(id+"F2.wireOp",EDGE,"E14"),sQuery(id+"F2.wireOp",EDGE,"E15"),sQuery(id+"F2.wireOp",EDGE,"E17"),sQuery(id+"F2.wireOp",EDGE,"E18"),sQuery(id+"F2.wireOp",EDGE,"E19"),sQuery(id+"F2.wireOp",EDGE,"E20.MirrorCS"),sQuery(id+"F2.wireOp",EDGE,"E21.MirrorCS"),sQuery(id+"F2.wireOp",EDGE,"E22.MirrorCS"),sQuery(id+"F2.wireOp",EDGE,"E23.MirrorCS"),sQuery(id+"F2.wireOp",EDGE,"E24.MirrorCS"),sQuery(id+"F2.wireOp",EDGE,"E25.MirrorCS")])],"isStart":false}),"instanceName":"1"})}),makeQuery(id+"F18.opPattern","COPY",FACE,{"derivedFrom":makeQuery(id+"F16.opExtrude","CAP_FACE",FACE,{"disambiguationData":[OSD([sQuery(id+"F15.wireOp",EDGE,"E27"),sQuery(id+"F15.wireOp",EDGE,"E28"),sQuery(id+"F15.wireOp",EDGE,"E29"),sQuery(id+"F15.wireOp",EDGE,"E30")])],"isStart":true}),"instanceName":"2"})]});
            var Q19;
            Q19=makeQuery(id+"F18.boolean.opBoolean","INTERSECT",EDGE,{"derivedFrom":[makeQuery(id+"F8.opChamfer","SPLIT",FACE,{"disambiguationData":[OD(0.0)],"derivedFrom":makeQuery(id+"F7.opPattern","COPY",FACE,{"derivedFrom":makeQuery(id+"F4.opExtrude","CAP_FACE",FACE,{"disambiguationData":[OSD([sQuery(id+"F2.wireOp",EDGE,"E9"),sQuery(id+"F2.wireOp",EDGE,"E10"),sQuery(id+"F2.wireOp",EDGE,"E11"),sQuery(id+"F2.wireOp",EDGE,"E12"),sQuery(id+"F2.wireOp",EDGE,"E13"),sQuery(id+"F2.wireOp",EDGE,"E14"),sQuery(id+"F2.wireOp",EDGE,"E15"),sQuery(id+"F2.wireOp",EDGE,"E17"),sQuery(id+"F2.wireOp",EDGE,"E18"),sQuery(id+"F2.wireOp",EDGE,"E19"),sQuery(id+"F2.wireOp",EDGE,"E20.MirrorCS"),sQuery(id+"F2.wireOp",EDGE,"E21.MirrorCS"),sQuery(id+"F2.wireOp",EDGE,"E22.MirrorCS"),sQuery(id+"F2.wireOp",EDGE,"E23.MirrorCS"),sQuery(id+"F2.wireOp",EDGE,"E24.MirrorCS"),sQuery(id+"F2.wireOp",EDGE,"E25.MirrorCS")])],"isStart":false}),"instanceName":"1"})}),makeQuery(id+"F18.opPattern","COPY",FACE,{"derivedFrom":makeQuery(id+"F16.opExtrude","CAP_FACE",FACE,{"disambiguationData":[OSD([sQuery(id+"F15.wireOp",EDGE,"E27"),sQuery(id+"F15.wireOp",EDGE,"E28"),sQuery(id+"F15.wireOp",EDGE,"E29"),sQuery(id+"F15.wireOp",EDGE,"E30")])],"isStart":false}),"instanceName":"2"})]});
            var Q20;
            Q20=makeQuery(id+"F18.boolean.opBoolean","INTERSECT",EDGE,{"derivedFrom":[makeQuery(id+"F8.opChamfer","SPLIT",FACE,{"disambiguationData":[OD(0.0)],"derivedFrom":makeQuery(id+"F7.opPattern","COPY",FACE,{"derivedFrom":makeQuery(id+"F4.opExtrude","CAP_FACE",FACE,{"disambiguationData":[OSD([sQuery(id+"F2.wireOp",EDGE,"E9"),sQuery(id+"F2.wireOp",EDGE,"E10"),sQuery(id+"F2.wireOp",EDGE,"E11"),sQuery(id+"F2.wireOp",EDGE,"E12"),sQuery(id+"F2.wireOp",EDGE,"E13"),sQuery(id+"F2.wireOp",EDGE,"E14"),sQuery(id+"F2.wireOp",EDGE,"E15"),sQuery(id+"F2.wireOp",EDGE,"E17"),sQuery(id+"F2.wireOp",EDGE,"E18"),sQuery(id+"F2.wireOp",EDGE,"E19"),sQuery(id+"F2.wireOp",EDGE,"E20.MirrorCS"),sQuery(id+"F2.wireOp",EDGE,"E21.MirrorCS"),sQuery(id+"F2.wireOp",EDGE,"E22.MirrorCS"),sQuery(id+"F2.wireOp",EDGE,"E23.MirrorCS"),sQuery(id+"F2.wireOp",EDGE,"E24.MirrorCS"),sQuery(id+"F2.wireOp",EDGE,"E25.MirrorCS")])],"isStart":false}),"instanceName":"1"})}),makeQuery(id+"F18.opPattern","COPY",FACE,{"derivedFrom":makeQuery(id+"F17.opPattern","COPY",FACE,{"derivedFrom":makeQuery(id+"F16.opExtrude","CAP_FACE",FACE,{"disambiguationData":[OSD([sQuery(id+"F15.wireOp",EDGE,"E27"),sQuery(id+"F15.wireOp",EDGE,"E28"),sQuery(id+"F15.wireOp",EDGE,"E29"),sQuery(id+"F15.wireOp",EDGE,"E30")])],"isStart":true}),"instanceName":"1"}),"instanceName":"2"})]});
            var Q21;
            Q21=makeQuery(id+"F18.boolean.opBoolean","INTERSECT",EDGE,{"derivedFrom":[makeQuery(id+"F8.opChamfer","SPLIT",FACE,{"disambiguationData":[OD(0.0)],"derivedFrom":makeQuery(id+"F7.opPattern","COPY",FACE,{"derivedFrom":makeQuery(id+"F4.opExtrude","CAP_FACE",FACE,{"disambiguationData":[OSD([sQuery(id+"F2.wireOp",EDGE,"E9"),sQuery(id+"F2.wireOp",EDGE,"E10"),sQuery(id+"F2.wireOp",EDGE,"E11"),sQuery(id+"F2.wireOp",EDGE,"E12"),sQuery(id+"F2.wireOp",EDGE,"E13"),sQuery(id+"F2.wireOp",EDGE,"E14"),sQuery(id+"F2.wireOp",EDGE,"E15"),sQuery(id+"F2.wireOp",EDGE,"E17"),sQuery(id+"F2.wireOp",EDGE,"E18"),sQuery(id+"F2.wireOp",EDGE,"E19"),sQuery(id+"F2.wireOp",EDGE,"E20.MirrorCS"),sQuery(id+"F2.wireOp",EDGE,"E21.MirrorCS"),sQuery(id+"F2.wireOp",EDGE,"E22.MirrorCS"),sQuery(id+"F2.wireOp",EDGE,"E23.MirrorCS"),sQuery(id+"F2.wireOp",EDGE,"E24.MirrorCS"),sQuery(id+"F2.wireOp",EDGE,"E25.MirrorCS")])],"isStart":false}),"instanceName":"1"})}),makeQuery(id+"F18.opPattern","COPY",FACE,{"derivedFrom":makeQuery(id+"F17.opPattern","COPY",FACE,{"derivedFrom":makeQuery(id+"F16.opExtrude","CAP_FACE",FACE,{"disambiguationData":[OSD([sQuery(id+"F15.wireOp",EDGE,"E27"),sQuery(id+"F15.wireOp",EDGE,"E28"),sQuery(id+"F15.wireOp",EDGE,"E29"),sQuery(id+"F15.wireOp",EDGE,"E30")])],"isStart":false}),"instanceName":"1"}),"instanceName":"2"})]});
            var Q22;
            {var subQ0=sQuery(id+"F2.wireOp",EDGE,"E10");Q22=makeQuery(id+"F18.boolean.opBoolean","INTERSECT",EDGE,{"derivedFrom":[makeQuery(id+"F10.opFillet","BLEND_FACE",FACE,{"disambiguationData":[OSD([subQ0]),TDD([makeQuery(id+"F7.opPattern","COPY",EDGE,{"derivedFrom":makeQuery(id+"F4.opExtrude","CAP_EDGE",EDGE,{"disambiguationData":[OSD([subQ0])],"isStart":false}),"instanceName":"1"})])]}),makeQuery(id+"F18.opPattern","COPY",FACE,{"derivedFrom":makeQuery(id+"F17.opPattern","COPY",FACE,{"derivedFrom":makeQuery(id+"F16.opExtrude","SWEPT_FACE",FACE,{"disambiguationData":[OSD([sQuery(id+"F15.wireOp",EDGE,"E30")])]}),"instanceName":"1"}),"instanceName":"2"})]});}
            var Q23;
            {var subQ0=sQuery(id+"F2.wireOp",EDGE,"E25.MirrorCS");var subQ1=sQuery(id+"F2.wireOp",EDGE,"E19");var subQ2=sQuery(id+"F2.wireOp",EDGE,"E13");Q23=makeQuery(id+"F18.boolean.opBoolean","INTERSECT",EDGE,{"derivedFrom":[makeQuery(id+"F9.opFillet","SPLIT",FACE,{"disambiguationData":[OD(0.0)],"derivedFrom":makeQuery(id+"F8.opChamfer","BLEND_FACE",FACE,{"disambiguationData":[OSD([subQ2,subQ1,subQ0]),TDD([makeQuery(id+"F7.opPattern","COPY",EDGE,{"derivedFrom":makeQuery(id+"F4.opExtrude","CAP_EDGE",EDGE,{"disambiguationData":[OSD([subQ2,subQ1,subQ0])],"isStart":false}),"instanceName":"1"})])]})}),makeQuery(id+"F18.opPattern","COPY",FACE,{"derivedFrom":makeQuery(id+"F17.opPattern","COPY",FACE,{"derivedFrom":makeQuery(id+"F16.opExtrude","SWEPT_FACE",FACE,{"disambiguationData":[OSD([sQuery(id+"F15.wireOp",EDGE,"E28")])]}),"instanceName":"1"}),"instanceName":"2"})]});}
            fillet(context, id + "F19", {"entities" : qUnion([Q0, Q1, Q2, Q3, Q4, Q5, Q6, Q7, Q8, Q9, Q10, Q11, Q12, Q13, Q14, Q15, Q16, Q17, Q18, Q19, Q20, Q21, Q22, Q23]), "radius" : 0.3 * mm, "tangentPropagation" : true, "allowEdgeOverflow" : false});
        }
    });
